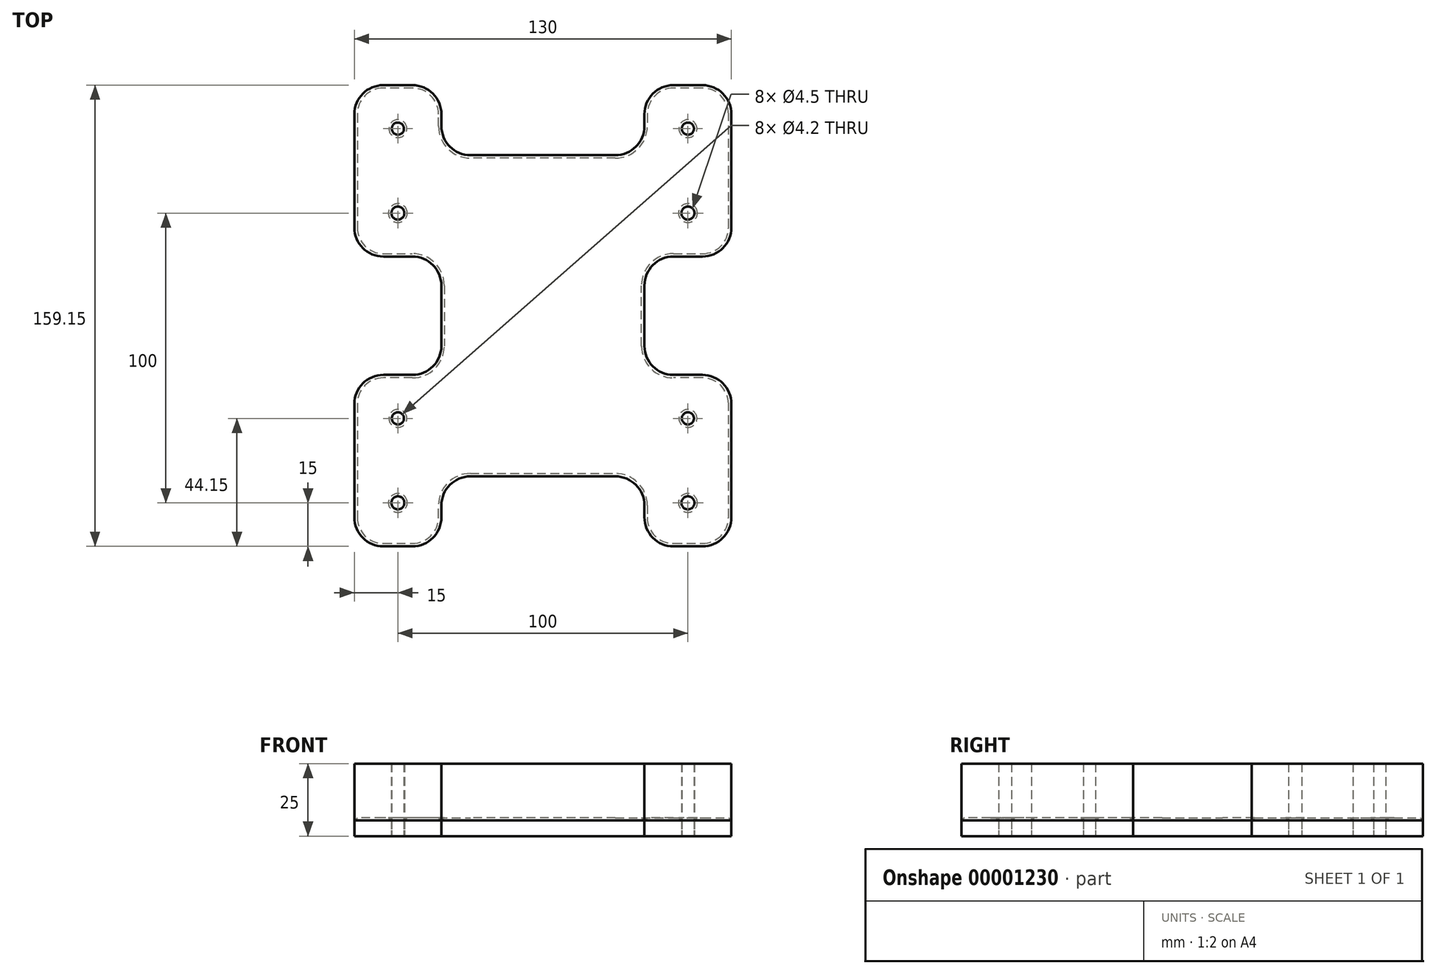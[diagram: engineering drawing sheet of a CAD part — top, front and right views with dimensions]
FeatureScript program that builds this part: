
annotation { "Feature Type Name" : "Feature", "Feature Type Description" : "" }
export const myFeature = defineFeature(function(context is Context, id is Id, definition is map)
    precondition{}
    {
        {
            var Q0;
            Q0=qCreatedBy(makeId("Top.planeOp"),FACE);
            var sketch = newSketch(context, id + "F0", { "sketchPlane" : qUnion([Q0])});
            skLineSegment(sketch, "E0", {"start": v(0, 159.15) * mm, "end": v(30, 159.15) * mm});
            skLineSegment(sketch, "E1", {"start": v(30, 159.15) * mm, "end": v(30, 135) * mm});
            skLineSegment(sketch, "E2", {"start": v(30, 135) * mm, "end": v(100, 135) * mm});
            skLineSegment(sketch, "E3", {"start": v(100, 135) * mm, "end": v(100, 159.15) * mm});
            skLineSegment(sketch, "E4", {"start": v(100, 159.15) * mm, "end": v(130, 159.15) * mm});
            skLineSegment(sketch, "E5", {"start": v(130, 159.15) * mm, "end": v(130, 100) * mm});
            skLineSegment(sketch, "E6", {"start": v(130, 100) * mm, "end": v(100, 100) * mm});
            skLineSegment(sketch, "E7", {"start": v(100, 100) * mm, "end": v(100, 59.15) * mm});
            skLineSegment(sketch, "E8", {"start": v(100, 59.15) * mm, "end": v(130, 59.15) * mm});
            skLineSegment(sketch, "E9", {"start": v(130, 59.15) * mm, "end": v(130, 0) * mm});
            skLineSegment(sketch, "E10", {"start": v(130, 0) * mm, "end": v(100, 0) * mm});
            skLineSegment(sketch, "E11", {"start": v(100, 0) * mm, "end": v(100, 24.15) * mm});
            skLineSegment(sketch, "E12", {"start": v(100, 24.15) * mm, "end": v(30, 24.15) * mm});
            skLineSegment(sketch, "E13", {"start": v(30, 24.15) * mm, "end": v(30, 0) * mm});
            skLineSegment(sketch, "E14", {"start": v(30, 0) * mm, "end": v(0, 0) * mm});
            skLineSegment(sketch, "E15", {"start": v(0, 0) * mm, "end": v(0, 59.15) * mm});
            skLineSegment(sketch, "E16", {"start": v(0, 59.15) * mm, "end": v(30, 59.15) * mm});
            skLineSegment(sketch, "E17", {"start": v(30, 59.15) * mm, "end": v(30, 100) * mm});
            skLineSegment(sketch, "E18", {"start": v(30, 100) * mm, "end": v(0, 100) * mm});
            skLineSegment(sketch, "E19", {"start": v(0, 100) * mm, "end": v(0, 159.15) * mm});
            skLineSegment(sketch, "E20", {"start": v(15, 159.15) * mm, "end": v(15, 144.15) * mm, "construction": true});
            skLineSegment(sketch, "E21", {"start": v(15, 100) * mm, "end": v(15, 115) * mm, "construction": true});
            skCircle(sketch, "E22", {"center": v(15, 144.15) * mm, "radius": 2.1 * mm});
            skCircle(sketch, "E23", {"center": v(15, 115) * mm, "radius": 2.25 * mm});
            skLineSegment(sketch, "E24", {"start": v(65, 135) * mm, "end": v(65, 24.15) * mm, "construction": true});
            skLineSegment(sketch, "E25", {"start": v(30, 79.57) * mm, "end": v(100, 79.57) * mm, "construction": true});
            skLineSegment(sketch, "E26", {"start": v(15, 59.15) * mm, "end": v(15, 44.15) * mm, "construction": true});
            skLineSegment(sketch, "E27", {"start": v(15, 0) * mm, "end": v(15, 15) * mm, "construction": true});
            skCircle(sketch, "E28", {"center": v(15, 44.15) * mm, "radius": 2.1 * mm});
            skCircle(sketch, "E29", {"center": v(15, 15) * mm, "radius": 2.25 * mm});
            skCircle(sketch, "E30.0.MirrorC", {"center": v(115, 15) * mm, "radius": 2.25 * mm});
            skCircle(sketch, "E30.1.MirrorC", {"center": v(115, 44.15) * mm, "radius": 2.1 * mm});
            skCircle(sketch, "E31.0.MirrorC", {"center": v(115, 115) * mm, "radius": 2.25 * mm});
            skCircle(sketch, "E31.1.MirrorC", {"center": v(115, 144.15) * mm, "radius": 2.1 * mm});
            skLineSegment(sketch, "E32", {"start": v(115, 144.15) * mm, "end": v(115, 44.15) * mm, "construction": true});
            skSolve(sketch);
        }
        {
            var Q0;
            Q0=makeQuery(id+"F0.imprint","IMPRINT",FACE,{"disambiguationData":[TD([[makeQuery(id+"F0.imprint","IMPRINT",EDGE,{"derivedFrom":sQuery(id+"F0.wireOp",EDGE,"E0")}),-1.0]])]});
            extrude(context, id + "F1", {"entities" : qUnion([Q0]), "depth" : 6.35 * mm});
        }
        {
            var Q0;
            Q0=makeQuery(id+"F1.opExtrude","SWEPT_EDGE",EDGE,{"disambiguationData":[OSD([sQuery(id+"F0.wireOp",EDGE,"E0"),sQuery(id+"F0.wireOp",EDGE,"E1")])]});
            var Q1;
            Q1=makeQuery(id+"F1.opExtrude","SWEPT_EDGE",EDGE,{"disambiguationData":[OSD([sQuery(id+"F0.wireOp",EDGE,"E0"),sQuery(id+"F0.wireOp",EDGE,"E19")])]});
            var Q2;
            Q2=makeQuery(id+"F1.opExtrude","SWEPT_EDGE",EDGE,{"disambiguationData":[OSD([sQuery(id+"F0.wireOp",EDGE,"E3"),sQuery(id+"F0.wireOp",EDGE,"E4")])]});
            var Q3;
            Q3=makeQuery(id+"F1.opExtrude","SWEPT_EDGE",EDGE,{"disambiguationData":[OSD([sQuery(id+"F0.wireOp",EDGE,"E4"),sQuery(id+"F0.wireOp",EDGE,"E5")])]});
            var Q4;
            Q4=makeQuery(id+"F1.opExtrude","SWEPT_EDGE",EDGE,{"disambiguationData":[OSD([sQuery(id+"F0.wireOp",EDGE,"E5"),sQuery(id+"F0.wireOp",EDGE,"E6")])]});
            var Q5;
            Q5=makeQuery(id+"F1.opExtrude","SWEPT_EDGE",EDGE,{"disambiguationData":[OSD([sQuery(id+"F0.wireOp",EDGE,"E7"),sQuery(id+"F0.wireOp",EDGE,"E8")])]});
            var Q6;
            Q6=makeQuery(id+"F1.opExtrude","SWEPT_EDGE",EDGE,{"disambiguationData":[OSD([sQuery(id+"F0.wireOp",EDGE,"E8"),sQuery(id+"F0.wireOp",EDGE,"E9")])]});
            var Q7;
            Q7=makeQuery(id+"F1.opExtrude","SWEPT_EDGE",EDGE,{"disambiguationData":[OSD([sQuery(id+"F0.wireOp",EDGE,"E9"),sQuery(id+"F0.wireOp",EDGE,"E10")])]});
            var Q8;
            Q8=makeQuery(id+"F1.opExtrude","SWEPT_EDGE",EDGE,{"disambiguationData":[OSD([sQuery(id+"F0.wireOp",EDGE,"E13"),sQuery(id+"F0.wireOp",EDGE,"E14")])]});
            var Q9;
            Q9=makeQuery(id+"F1.opExtrude","SWEPT_EDGE",EDGE,{"disambiguationData":[OSD([sQuery(id+"F0.wireOp",EDGE,"E15"),sQuery(id+"F0.wireOp",EDGE,"E16")])]});
            var Q10;
            Q10=makeQuery(id+"F1.opExtrude","SWEPT_EDGE",EDGE,{"disambiguationData":[OSD([sQuery(id+"F0.wireOp",EDGE,"E1"),sQuery(id+"F0.wireOp",EDGE,"E2")])]});
            var Q11;
            Q11=makeQuery(id+"F1.opExtrude","SWEPT_EDGE",EDGE,{"disambiguationData":[OSD([sQuery(id+"F0.wireOp",EDGE,"E2"),sQuery(id+"F0.wireOp",EDGE,"E3")])]});
            var Q12;
            Q12=makeQuery(id+"F1.opExtrude","SWEPT_EDGE",EDGE,{"disambiguationData":[OSD([sQuery(id+"F0.wireOp",EDGE,"E18"),sQuery(id+"F0.wireOp",EDGE,"E19")])]});
            var Q13;
            Q13=makeQuery(id+"F1.opExtrude","SWEPT_EDGE",EDGE,{"disambiguationData":[OSD([sQuery(id+"F0.wireOp",EDGE,"E10"),sQuery(id+"F0.wireOp",EDGE,"E11")])]});
            var Q14;
            Q14=makeQuery(id+"F1.opExtrude","SWEPT_EDGE",EDGE,{"disambiguationData":[OSD([sQuery(id+"F0.wireOp",EDGE,"E14"),sQuery(id+"F0.wireOp",EDGE,"E15")])]});
            var Q15;
            Q15=makeQuery(id+"F1.opExtrude","SWEPT_EDGE",EDGE,{"disambiguationData":[OSD([sQuery(id+"F0.wireOp",EDGE,"E16"),sQuery(id+"F0.wireOp",EDGE,"E17")])]});
            var Q16;
            Q16=makeQuery(id+"F1.opExtrude","SWEPT_EDGE",EDGE,{"disambiguationData":[OSD([sQuery(id+"F0.wireOp",EDGE,"E12"),sQuery(id+"F0.wireOp",EDGE,"E13")])]});
            var Q17;
            Q17=makeQuery(id+"F1.opExtrude","SWEPT_EDGE",EDGE,{"disambiguationData":[OSD([sQuery(id+"F0.wireOp",EDGE,"E6"),sQuery(id+"F0.wireOp",EDGE,"E7")])]});
            var Q18;
            Q18=makeQuery(id+"F1.opExtrude","SWEPT_EDGE",EDGE,{"disambiguationData":[OSD([sQuery(id+"F0.wireOp",EDGE,"E11"),sQuery(id+"F0.wireOp",EDGE,"E12")])]});
            var Q19;
            Q19=makeQuery(id+"F1.opExtrude","SWEPT_EDGE",EDGE,{"disambiguationData":[OSD([sQuery(id+"F0.wireOp",EDGE,"E17"),sQuery(id+"F0.wireOp",EDGE,"E18")])]});
            fillet(context, id + "F2", {"entities" : qUnion([Q0, Q1, Q2, Q3, Q4, Q5, Q6, Q7, Q8, Q9, Q10, Q11, Q12, Q13, Q14, Q15, Q16, Q17, Q18, Q19]), "radius" : 10 * mm, "tangentPropagation" : true, "allowEdgeOverflow" : false});
        }
        {
            var Q0;
            Q0=makeQuery(id+"F1.opExtrude","CAP_EDGE",EDGE,{"disambiguationData":[OSD([sQuery(id+"F0.wireOp",EDGE,"E12")])],"isStart":false});
            var Q1;
            {var subQ0=sQuery(id+"F0.wireOp",EDGE,"E13");var subQ1=sQuery(id+"F0.wireOp",EDGE,"E14");Q1=makeQuery(id+"F2.opFillet","BLEND_EDGE",EDGE,{"blendedFrom":[makeQuery(id+"F1.opExtrude","SWEPT_EDGE",EDGE,{"disambiguationData":[OSD([subQ0,subQ1])]}),makeQuery(id+"F1.opExtrude","CAP_FACE",FACE,{"disambiguationData":[OSD([sQuery(id+"F0.wireOp",EDGE,"E0"),sQuery(id+"F0.wireOp",EDGE,"E1"),sQuery(id+"F0.wireOp",EDGE,"E2"),sQuery(id+"F0.wireOp",EDGE,"E3"),sQuery(id+"F0.wireOp",EDGE,"E4"),sQuery(id+"F0.wireOp",EDGE,"E5"),sQuery(id+"F0.wireOp",EDGE,"E6"),sQuery(id+"F0.wireOp",EDGE,"E7"),sQuery(id+"F0.wireOp",EDGE,"E8"),sQuery(id+"F0.wireOp",EDGE,"E9"),sQuery(id+"F0.wireOp",EDGE,"E10"),sQuery(id+"F0.wireOp",EDGE,"E11"),sQuery(id+"F0.wireOp",EDGE,"E12"),subQ0,subQ1,sQuery(id+"F0.wireOp",EDGE,"E15"),sQuery(id+"F0.wireOp",EDGE,"E16"),sQuery(id+"F0.wireOp",EDGE,"E17"),sQuery(id+"F0.wireOp",EDGE,"E18"),sQuery(id+"F0.wireOp",EDGE,"E19"),sQuery(id+"F0.wireOp",EDGE,"E22"),sQuery(id+"F0.wireOp",EDGE,"E23"),sQuery(id+"F0.wireOp",EDGE,"E28"),sQuery(id+"F0.wireOp",EDGE,"E29"),sQuery(id+"F0.wireOp",EDGE,"E30.0.MirrorC"),sQuery(id+"F0.wireOp",EDGE,"E30.1.MirrorC"),sQuery(id+"F0.wireOp",EDGE,"E31.0.MirrorC"),sQuery(id+"F0.wireOp",EDGE,"E31.1.MirrorC")])],"isStart":false})],"blendedInto":[makeQuery(id+"F1.opExtrude","CAP_FACE",FACE,{"disambiguationData":[OSD([sQuery(id+"F0.wireOp",EDGE,"E0"),sQuery(id+"F0.wireOp",EDGE,"E1"),sQuery(id+"F0.wireOp",EDGE,"E2"),sQuery(id+"F0.wireOp",EDGE,"E3"),sQuery(id+"F0.wireOp",EDGE,"E4"),sQuery(id+"F0.wireOp",EDGE,"E5"),sQuery(id+"F0.wireOp",EDGE,"E6"),sQuery(id+"F0.wireOp",EDGE,"E7"),sQuery(id+"F0.wireOp",EDGE,"E8"),sQuery(id+"F0.wireOp",EDGE,"E9"),sQuery(id+"F0.wireOp",EDGE,"E10"),sQuery(id+"F0.wireOp",EDGE,"E11"),sQuery(id+"F0.wireOp",EDGE,"E12"),subQ0,subQ1,sQuery(id+"F0.wireOp",EDGE,"E15"),sQuery(id+"F0.wireOp",EDGE,"E16"),sQuery(id+"F0.wireOp",EDGE,"E17"),sQuery(id+"F0.wireOp",EDGE,"E18"),sQuery(id+"F0.wireOp",EDGE,"E19"),sQuery(id+"F0.wireOp",EDGE,"E22"),sQuery(id+"F0.wireOp",EDGE,"E23"),sQuery(id+"F0.wireOp",EDGE,"E28"),sQuery(id+"F0.wireOp",EDGE,"E29"),sQuery(id+"F0.wireOp",EDGE,"E30.0.MirrorC"),sQuery(id+"F0.wireOp",EDGE,"E30.1.MirrorC"),sQuery(id+"F0.wireOp",EDGE,"E31.0.MirrorC"),sQuery(id+"F0.wireOp",EDGE,"E31.1.MirrorC")])],"isStart":false})]});}
            var Q2;
            {var subQ0=sQuery(id+"F0.wireOp",EDGE,"E10");var subQ1=sQuery(id+"F0.wireOp",EDGE,"E11");Q2=makeQuery(id+"F2.opFillet","BLEND_EDGE",EDGE,{"blendedFrom":[makeQuery(id+"F1.opExtrude","SWEPT_EDGE",EDGE,{"disambiguationData":[OSD([subQ0,subQ1])]}),makeQuery(id+"F1.opExtrude","CAP_FACE",FACE,{"disambiguationData":[OSD([sQuery(id+"F0.wireOp",EDGE,"E0"),sQuery(id+"F0.wireOp",EDGE,"E1"),sQuery(id+"F0.wireOp",EDGE,"E2"),sQuery(id+"F0.wireOp",EDGE,"E3"),sQuery(id+"F0.wireOp",EDGE,"E4"),sQuery(id+"F0.wireOp",EDGE,"E5"),sQuery(id+"F0.wireOp",EDGE,"E6"),sQuery(id+"F0.wireOp",EDGE,"E7"),sQuery(id+"F0.wireOp",EDGE,"E8"),sQuery(id+"F0.wireOp",EDGE,"E9"),subQ0,subQ1,sQuery(id+"F0.wireOp",EDGE,"E12"),sQuery(id+"F0.wireOp",EDGE,"E13"),sQuery(id+"F0.wireOp",EDGE,"E14"),sQuery(id+"F0.wireOp",EDGE,"E15"),sQuery(id+"F0.wireOp",EDGE,"E16"),sQuery(id+"F0.wireOp",EDGE,"E17"),sQuery(id+"F0.wireOp",EDGE,"E18"),sQuery(id+"F0.wireOp",EDGE,"E19"),sQuery(id+"F0.wireOp",EDGE,"E22"),sQuery(id+"F0.wireOp",EDGE,"E23"),sQuery(id+"F0.wireOp",EDGE,"E28"),sQuery(id+"F0.wireOp",EDGE,"E29"),sQuery(id+"F0.wireOp",EDGE,"E30.0.MirrorC"),sQuery(id+"F0.wireOp",EDGE,"E30.1.MirrorC"),sQuery(id+"F0.wireOp",EDGE,"E31.0.MirrorC"),sQuery(id+"F0.wireOp",EDGE,"E31.1.MirrorC")])],"isStart":false})],"blendedInto":[makeQuery(id+"F1.opExtrude","CAP_FACE",FACE,{"disambiguationData":[OSD([sQuery(id+"F0.wireOp",EDGE,"E0"),sQuery(id+"F0.wireOp",EDGE,"E1"),sQuery(id+"F0.wireOp",EDGE,"E2"),sQuery(id+"F0.wireOp",EDGE,"E3"),sQuery(id+"F0.wireOp",EDGE,"E4"),sQuery(id+"F0.wireOp",EDGE,"E5"),sQuery(id+"F0.wireOp",EDGE,"E6"),sQuery(id+"F0.wireOp",EDGE,"E7"),sQuery(id+"F0.wireOp",EDGE,"E8"),sQuery(id+"F0.wireOp",EDGE,"E9"),subQ0,subQ1,sQuery(id+"F0.wireOp",EDGE,"E12"),sQuery(id+"F0.wireOp",EDGE,"E13"),sQuery(id+"F0.wireOp",EDGE,"E14"),sQuery(id+"F0.wireOp",EDGE,"E15"),sQuery(id+"F0.wireOp",EDGE,"E16"),sQuery(id+"F0.wireOp",EDGE,"E17"),sQuery(id+"F0.wireOp",EDGE,"E18"),sQuery(id+"F0.wireOp",EDGE,"E19"),sQuery(id+"F0.wireOp",EDGE,"E22"),sQuery(id+"F0.wireOp",EDGE,"E23"),sQuery(id+"F0.wireOp",EDGE,"E28"),sQuery(id+"F0.wireOp",EDGE,"E29"),sQuery(id+"F0.wireOp",EDGE,"E30.0.MirrorC"),sQuery(id+"F0.wireOp",EDGE,"E30.1.MirrorC"),sQuery(id+"F0.wireOp",EDGE,"E31.0.MirrorC"),sQuery(id+"F0.wireOp",EDGE,"E31.1.MirrorC")])],"isStart":false})]});}
            var Q3;
            {var subQ0=sQuery(id+"F0.wireOp",EDGE,"E9");var subQ1=sQuery(id+"F0.wireOp",EDGE,"E10");Q3=makeQuery(id+"F2.opFillet","BLEND_EDGE",EDGE,{"blendedFrom":[makeQuery(id+"F1.opExtrude","SWEPT_EDGE",EDGE,{"disambiguationData":[OSD([subQ0,subQ1])]}),makeQuery(id+"F1.opExtrude","CAP_FACE",FACE,{"disambiguationData":[OSD([sQuery(id+"F0.wireOp",EDGE,"E0"),sQuery(id+"F0.wireOp",EDGE,"E1"),sQuery(id+"F0.wireOp",EDGE,"E2"),sQuery(id+"F0.wireOp",EDGE,"E3"),sQuery(id+"F0.wireOp",EDGE,"E4"),sQuery(id+"F0.wireOp",EDGE,"E5"),sQuery(id+"F0.wireOp",EDGE,"E6"),sQuery(id+"F0.wireOp",EDGE,"E7"),sQuery(id+"F0.wireOp",EDGE,"E8"),subQ0,subQ1,sQuery(id+"F0.wireOp",EDGE,"E11"),sQuery(id+"F0.wireOp",EDGE,"E12"),sQuery(id+"F0.wireOp",EDGE,"E13"),sQuery(id+"F0.wireOp",EDGE,"E14"),sQuery(id+"F0.wireOp",EDGE,"E15"),sQuery(id+"F0.wireOp",EDGE,"E16"),sQuery(id+"F0.wireOp",EDGE,"E17"),sQuery(id+"F0.wireOp",EDGE,"E18"),sQuery(id+"F0.wireOp",EDGE,"E19"),sQuery(id+"F0.wireOp",EDGE,"E22"),sQuery(id+"F0.wireOp",EDGE,"E23"),sQuery(id+"F0.wireOp",EDGE,"E28"),sQuery(id+"F0.wireOp",EDGE,"E29"),sQuery(id+"F0.wireOp",EDGE,"E30.0.MirrorC"),sQuery(id+"F0.wireOp",EDGE,"E30.1.MirrorC"),sQuery(id+"F0.wireOp",EDGE,"E31.0.MirrorC"),sQuery(id+"F0.wireOp",EDGE,"E31.1.MirrorC")])],"isStart":false})],"blendedInto":[makeQuery(id+"F1.opExtrude","CAP_FACE",FACE,{"disambiguationData":[OSD([sQuery(id+"F0.wireOp",EDGE,"E0"),sQuery(id+"F0.wireOp",EDGE,"E1"),sQuery(id+"F0.wireOp",EDGE,"E2"),sQuery(id+"F0.wireOp",EDGE,"E3"),sQuery(id+"F0.wireOp",EDGE,"E4"),sQuery(id+"F0.wireOp",EDGE,"E5"),sQuery(id+"F0.wireOp",EDGE,"E6"),sQuery(id+"F0.wireOp",EDGE,"E7"),sQuery(id+"F0.wireOp",EDGE,"E8"),subQ0,subQ1,sQuery(id+"F0.wireOp",EDGE,"E11"),sQuery(id+"F0.wireOp",EDGE,"E12"),sQuery(id+"F0.wireOp",EDGE,"E13"),sQuery(id+"F0.wireOp",EDGE,"E14"),sQuery(id+"F0.wireOp",EDGE,"E15"),sQuery(id+"F0.wireOp",EDGE,"E16"),sQuery(id+"F0.wireOp",EDGE,"E17"),sQuery(id+"F0.wireOp",EDGE,"E18"),sQuery(id+"F0.wireOp",EDGE,"E19"),sQuery(id+"F0.wireOp",EDGE,"E22"),sQuery(id+"F0.wireOp",EDGE,"E23"),sQuery(id+"F0.wireOp",EDGE,"E28"),sQuery(id+"F0.wireOp",EDGE,"E29"),sQuery(id+"F0.wireOp",EDGE,"E30.0.MirrorC"),sQuery(id+"F0.wireOp",EDGE,"E30.1.MirrorC"),sQuery(id+"F0.wireOp",EDGE,"E31.0.MirrorC"),sQuery(id+"F0.wireOp",EDGE,"E31.1.MirrorC")])],"isStart":false})]});}
            var Q4;
            {var subQ0=sQuery(id+"F0.wireOp",EDGE,"E11");var subQ1=sQuery(id+"F0.wireOp",EDGE,"E12");Q4=makeQuery(id+"F2.opFillet","BLEND_EDGE",EDGE,{"blendedFrom":[makeQuery(id+"F1.opExtrude","SWEPT_EDGE",EDGE,{"disambiguationData":[OSD([subQ0,subQ1])]}),makeQuery(id+"F1.opExtrude","CAP_FACE",FACE,{"disambiguationData":[OSD([sQuery(id+"F0.wireOp",EDGE,"E0"),sQuery(id+"F0.wireOp",EDGE,"E1"),sQuery(id+"F0.wireOp",EDGE,"E2"),sQuery(id+"F0.wireOp",EDGE,"E3"),sQuery(id+"F0.wireOp",EDGE,"E4"),sQuery(id+"F0.wireOp",EDGE,"E5"),sQuery(id+"F0.wireOp",EDGE,"E6"),sQuery(id+"F0.wireOp",EDGE,"E7"),sQuery(id+"F0.wireOp",EDGE,"E8"),sQuery(id+"F0.wireOp",EDGE,"E9"),sQuery(id+"F0.wireOp",EDGE,"E10"),subQ0,subQ1,sQuery(id+"F0.wireOp",EDGE,"E13"),sQuery(id+"F0.wireOp",EDGE,"E14"),sQuery(id+"F0.wireOp",EDGE,"E15"),sQuery(id+"F0.wireOp",EDGE,"E16"),sQuery(id+"F0.wireOp",EDGE,"E17"),sQuery(id+"F0.wireOp",EDGE,"E18"),sQuery(id+"F0.wireOp",EDGE,"E19"),sQuery(id+"F0.wireOp",EDGE,"E22"),sQuery(id+"F0.wireOp",EDGE,"E23"),sQuery(id+"F0.wireOp",EDGE,"E28"),sQuery(id+"F0.wireOp",EDGE,"E29"),sQuery(id+"F0.wireOp",EDGE,"E30.0.MirrorC"),sQuery(id+"F0.wireOp",EDGE,"E30.1.MirrorC"),sQuery(id+"F0.wireOp",EDGE,"E31.0.MirrorC"),sQuery(id+"F0.wireOp",EDGE,"E31.1.MirrorC")])],"isStart":false})],"blendedInto":[makeQuery(id+"F1.opExtrude","CAP_FACE",FACE,{"disambiguationData":[OSD([sQuery(id+"F0.wireOp",EDGE,"E0"),sQuery(id+"F0.wireOp",EDGE,"E1"),sQuery(id+"F0.wireOp",EDGE,"E2"),sQuery(id+"F0.wireOp",EDGE,"E3"),sQuery(id+"F0.wireOp",EDGE,"E4"),sQuery(id+"F0.wireOp",EDGE,"E5"),sQuery(id+"F0.wireOp",EDGE,"E6"),sQuery(id+"F0.wireOp",EDGE,"E7"),sQuery(id+"F0.wireOp",EDGE,"E8"),sQuery(id+"F0.wireOp",EDGE,"E9"),sQuery(id+"F0.wireOp",EDGE,"E10"),subQ0,subQ1,sQuery(id+"F0.wireOp",EDGE,"E13"),sQuery(id+"F0.wireOp",EDGE,"E14"),sQuery(id+"F0.wireOp",EDGE,"E15"),sQuery(id+"F0.wireOp",EDGE,"E16"),sQuery(id+"F0.wireOp",EDGE,"E17"),sQuery(id+"F0.wireOp",EDGE,"E18"),sQuery(id+"F0.wireOp",EDGE,"E19"),sQuery(id+"F0.wireOp",EDGE,"E22"),sQuery(id+"F0.wireOp",EDGE,"E23"),sQuery(id+"F0.wireOp",EDGE,"E28"),sQuery(id+"F0.wireOp",EDGE,"E29"),sQuery(id+"F0.wireOp",EDGE,"E30.0.MirrorC"),sQuery(id+"F0.wireOp",EDGE,"E30.1.MirrorC"),sQuery(id+"F0.wireOp",EDGE,"E31.0.MirrorC"),sQuery(id+"F0.wireOp",EDGE,"E31.1.MirrorC")])],"isStart":false})]});}
            var Q5;
            {var subQ0=sQuery(id+"F0.wireOp",EDGE,"E14");var subQ1=sQuery(id+"F0.wireOp",EDGE,"E15");Q5=makeQuery(id+"F2.opFillet","BLEND_EDGE",EDGE,{"blendedFrom":[makeQuery(id+"F1.opExtrude","SWEPT_EDGE",EDGE,{"disambiguationData":[OSD([subQ0,subQ1])]}),makeQuery(id+"F1.opExtrude","CAP_FACE",FACE,{"disambiguationData":[OSD([sQuery(id+"F0.wireOp",EDGE,"E0"),sQuery(id+"F0.wireOp",EDGE,"E1"),sQuery(id+"F0.wireOp",EDGE,"E2"),sQuery(id+"F0.wireOp",EDGE,"E3"),sQuery(id+"F0.wireOp",EDGE,"E4"),sQuery(id+"F0.wireOp",EDGE,"E5"),sQuery(id+"F0.wireOp",EDGE,"E6"),sQuery(id+"F0.wireOp",EDGE,"E7"),sQuery(id+"F0.wireOp",EDGE,"E8"),sQuery(id+"F0.wireOp",EDGE,"E9"),sQuery(id+"F0.wireOp",EDGE,"E10"),sQuery(id+"F0.wireOp",EDGE,"E11"),sQuery(id+"F0.wireOp",EDGE,"E12"),sQuery(id+"F0.wireOp",EDGE,"E13"),subQ0,subQ1,sQuery(id+"F0.wireOp",EDGE,"E16"),sQuery(id+"F0.wireOp",EDGE,"E17"),sQuery(id+"F0.wireOp",EDGE,"E18"),sQuery(id+"F0.wireOp",EDGE,"E19"),sQuery(id+"F0.wireOp",EDGE,"E22"),sQuery(id+"F0.wireOp",EDGE,"E23"),sQuery(id+"F0.wireOp",EDGE,"E28"),sQuery(id+"F0.wireOp",EDGE,"E29"),sQuery(id+"F0.wireOp",EDGE,"E30.0.MirrorC"),sQuery(id+"F0.wireOp",EDGE,"E30.1.MirrorC"),sQuery(id+"F0.wireOp",EDGE,"E31.0.MirrorC"),sQuery(id+"F0.wireOp",EDGE,"E31.1.MirrorC")])],"isStart":false})],"blendedInto":[makeQuery(id+"F1.opExtrude","CAP_FACE",FACE,{"disambiguationData":[OSD([sQuery(id+"F0.wireOp",EDGE,"E0"),sQuery(id+"F0.wireOp",EDGE,"E1"),sQuery(id+"F0.wireOp",EDGE,"E2"),sQuery(id+"F0.wireOp",EDGE,"E3"),sQuery(id+"F0.wireOp",EDGE,"E4"),sQuery(id+"F0.wireOp",EDGE,"E5"),sQuery(id+"F0.wireOp",EDGE,"E6"),sQuery(id+"F0.wireOp",EDGE,"E7"),sQuery(id+"F0.wireOp",EDGE,"E8"),sQuery(id+"F0.wireOp",EDGE,"E9"),sQuery(id+"F0.wireOp",EDGE,"E10"),sQuery(id+"F0.wireOp",EDGE,"E11"),sQuery(id+"F0.wireOp",EDGE,"E12"),sQuery(id+"F0.wireOp",EDGE,"E13"),subQ0,subQ1,sQuery(id+"F0.wireOp",EDGE,"E16"),sQuery(id+"F0.wireOp",EDGE,"E17"),sQuery(id+"F0.wireOp",EDGE,"E18"),sQuery(id+"F0.wireOp",EDGE,"E19"),sQuery(id+"F0.wireOp",EDGE,"E22"),sQuery(id+"F0.wireOp",EDGE,"E23"),sQuery(id+"F0.wireOp",EDGE,"E28"),sQuery(id+"F0.wireOp",EDGE,"E29"),sQuery(id+"F0.wireOp",EDGE,"E30.0.MirrorC"),sQuery(id+"F0.wireOp",EDGE,"E30.1.MirrorC"),sQuery(id+"F0.wireOp",EDGE,"E31.0.MirrorC"),sQuery(id+"F0.wireOp",EDGE,"E31.1.MirrorC")])],"isStart":false})]});}
            var Q6;
            Q6=makeQuery(id+"F1.opExtrude","CAP_EDGE",EDGE,{"disambiguationData":[OSD([sQuery(id+"F0.wireOp",EDGE,"E14")])],"isStart":false});
            var Q7;
            Q7=makeQuery(id+"F1.opExtrude","CAP_EDGE",EDGE,{"disambiguationData":[OSD([sQuery(id+"F0.wireOp",EDGE,"E10")])],"isStart":false});
            var Q8;
            {var subQ0=sQuery(id+"F0.wireOp",EDGE,"E12");var subQ1=sQuery(id+"F0.wireOp",EDGE,"E13");Q8=makeQuery(id+"F2.opFillet","BLEND_EDGE",EDGE,{"blendedFrom":[makeQuery(id+"F1.opExtrude","SWEPT_EDGE",EDGE,{"disambiguationData":[OSD([subQ0,subQ1])]}),makeQuery(id+"F1.opExtrude","CAP_FACE",FACE,{"disambiguationData":[OSD([sQuery(id+"F0.wireOp",EDGE,"E0"),sQuery(id+"F0.wireOp",EDGE,"E1"),sQuery(id+"F0.wireOp",EDGE,"E2"),sQuery(id+"F0.wireOp",EDGE,"E3"),sQuery(id+"F0.wireOp",EDGE,"E4"),sQuery(id+"F0.wireOp",EDGE,"E5"),sQuery(id+"F0.wireOp",EDGE,"E6"),sQuery(id+"F0.wireOp",EDGE,"E7"),sQuery(id+"F0.wireOp",EDGE,"E8"),sQuery(id+"F0.wireOp",EDGE,"E9"),sQuery(id+"F0.wireOp",EDGE,"E10"),sQuery(id+"F0.wireOp",EDGE,"E11"),subQ0,subQ1,sQuery(id+"F0.wireOp",EDGE,"E14"),sQuery(id+"F0.wireOp",EDGE,"E15"),sQuery(id+"F0.wireOp",EDGE,"E16"),sQuery(id+"F0.wireOp",EDGE,"E17"),sQuery(id+"F0.wireOp",EDGE,"E18"),sQuery(id+"F0.wireOp",EDGE,"E19"),sQuery(id+"F0.wireOp",EDGE,"E22"),sQuery(id+"F0.wireOp",EDGE,"E23"),sQuery(id+"F0.wireOp",EDGE,"E28"),sQuery(id+"F0.wireOp",EDGE,"E29"),sQuery(id+"F0.wireOp",EDGE,"E30.0.MirrorC"),sQuery(id+"F0.wireOp",EDGE,"E30.1.MirrorC"),sQuery(id+"F0.wireOp",EDGE,"E31.0.MirrorC"),sQuery(id+"F0.wireOp",EDGE,"E31.1.MirrorC")])],"isStart":false})],"blendedInto":[makeQuery(id+"F1.opExtrude","CAP_FACE",FACE,{"disambiguationData":[OSD([sQuery(id+"F0.wireOp",EDGE,"E0"),sQuery(id+"F0.wireOp",EDGE,"E1"),sQuery(id+"F0.wireOp",EDGE,"E2"),sQuery(id+"F0.wireOp",EDGE,"E3"),sQuery(id+"F0.wireOp",EDGE,"E4"),sQuery(id+"F0.wireOp",EDGE,"E5"),sQuery(id+"F0.wireOp",EDGE,"E6"),sQuery(id+"F0.wireOp",EDGE,"E7"),sQuery(id+"F0.wireOp",EDGE,"E8"),sQuery(id+"F0.wireOp",EDGE,"E9"),sQuery(id+"F0.wireOp",EDGE,"E10"),sQuery(id+"F0.wireOp",EDGE,"E11"),subQ0,subQ1,sQuery(id+"F0.wireOp",EDGE,"E14"),sQuery(id+"F0.wireOp",EDGE,"E15"),sQuery(id+"F0.wireOp",EDGE,"E16"),sQuery(id+"F0.wireOp",EDGE,"E17"),sQuery(id+"F0.wireOp",EDGE,"E18"),sQuery(id+"F0.wireOp",EDGE,"E19"),sQuery(id+"F0.wireOp",EDGE,"E22"),sQuery(id+"F0.wireOp",EDGE,"E23"),sQuery(id+"F0.wireOp",EDGE,"E28"),sQuery(id+"F0.wireOp",EDGE,"E29"),sQuery(id+"F0.wireOp",EDGE,"E30.0.MirrorC"),sQuery(id+"F0.wireOp",EDGE,"E30.1.MirrorC"),sQuery(id+"F0.wireOp",EDGE,"E31.0.MirrorC"),sQuery(id+"F0.wireOp",EDGE,"E31.1.MirrorC")])],"isStart":false})]});}
            var Q9;
            Q9=makeQuery(id+"F1.opExtrude","CAP_EDGE",EDGE,{"disambiguationData":[OSD([sQuery(id+"F0.wireOp",EDGE,"E30.0.MirrorC")])],"isStart":false});
            var Q10;
            Q10=makeQuery(id+"F1.opExtrude","CAP_EDGE",EDGE,{"disambiguationData":[OSD([sQuery(id+"F0.wireOp",EDGE,"E16")])],"isStart":false});
            var Q11;
            {var subQ0=sQuery(id+"F0.wireOp",EDGE,"E8");var subQ1=sQuery(id+"F0.wireOp",EDGE,"E9");Q11=makeQuery(id+"F2.opFillet","BLEND_EDGE",EDGE,{"blendedFrom":[makeQuery(id+"F1.opExtrude","SWEPT_EDGE",EDGE,{"disambiguationData":[OSD([subQ0,subQ1])]}),makeQuery(id+"F1.opExtrude","CAP_FACE",FACE,{"disambiguationData":[OSD([sQuery(id+"F0.wireOp",EDGE,"E0"),sQuery(id+"F0.wireOp",EDGE,"E1"),sQuery(id+"F0.wireOp",EDGE,"E2"),sQuery(id+"F0.wireOp",EDGE,"E3"),sQuery(id+"F0.wireOp",EDGE,"E4"),sQuery(id+"F0.wireOp",EDGE,"E5"),sQuery(id+"F0.wireOp",EDGE,"E6"),sQuery(id+"F0.wireOp",EDGE,"E7"),subQ0,subQ1,sQuery(id+"F0.wireOp",EDGE,"E10"),sQuery(id+"F0.wireOp",EDGE,"E11"),sQuery(id+"F0.wireOp",EDGE,"E12"),sQuery(id+"F0.wireOp",EDGE,"E13"),sQuery(id+"F0.wireOp",EDGE,"E14"),sQuery(id+"F0.wireOp",EDGE,"E15"),sQuery(id+"F0.wireOp",EDGE,"E16"),sQuery(id+"F0.wireOp",EDGE,"E17"),sQuery(id+"F0.wireOp",EDGE,"E18"),sQuery(id+"F0.wireOp",EDGE,"E19"),sQuery(id+"F0.wireOp",EDGE,"E22"),sQuery(id+"F0.wireOp",EDGE,"E23"),sQuery(id+"F0.wireOp",EDGE,"E28"),sQuery(id+"F0.wireOp",EDGE,"E29"),sQuery(id+"F0.wireOp",EDGE,"E30.0.MirrorC"),sQuery(id+"F0.wireOp",EDGE,"E30.1.MirrorC"),sQuery(id+"F0.wireOp",EDGE,"E31.0.MirrorC"),sQuery(id+"F0.wireOp",EDGE,"E31.1.MirrorC")])],"isStart":false})],"blendedInto":[makeQuery(id+"F1.opExtrude","CAP_FACE",FACE,{"disambiguationData":[OSD([sQuery(id+"F0.wireOp",EDGE,"E0"),sQuery(id+"F0.wireOp",EDGE,"E1"),sQuery(id+"F0.wireOp",EDGE,"E2"),sQuery(id+"F0.wireOp",EDGE,"E3"),sQuery(id+"F0.wireOp",EDGE,"E4"),sQuery(id+"F0.wireOp",EDGE,"E5"),sQuery(id+"F0.wireOp",EDGE,"E6"),sQuery(id+"F0.wireOp",EDGE,"E7"),subQ0,subQ1,sQuery(id+"F0.wireOp",EDGE,"E10"),sQuery(id+"F0.wireOp",EDGE,"E11"),sQuery(id+"F0.wireOp",EDGE,"E12"),sQuery(id+"F0.wireOp",EDGE,"E13"),sQuery(id+"F0.wireOp",EDGE,"E14"),sQuery(id+"F0.wireOp",EDGE,"E15"),sQuery(id+"F0.wireOp",EDGE,"E16"),sQuery(id+"F0.wireOp",EDGE,"E17"),sQuery(id+"F0.wireOp",EDGE,"E18"),sQuery(id+"F0.wireOp",EDGE,"E19"),sQuery(id+"F0.wireOp",EDGE,"E22"),sQuery(id+"F0.wireOp",EDGE,"E23"),sQuery(id+"F0.wireOp",EDGE,"E28"),sQuery(id+"F0.wireOp",EDGE,"E29"),sQuery(id+"F0.wireOp",EDGE,"E30.0.MirrorC"),sQuery(id+"F0.wireOp",EDGE,"E30.1.MirrorC"),sQuery(id+"F0.wireOp",EDGE,"E31.0.MirrorC"),sQuery(id+"F0.wireOp",EDGE,"E31.1.MirrorC")])],"isStart":false})]});}
            var Q12;
            Q12=makeQuery(id+"F1.opExtrude","CAP_EDGE",EDGE,{"disambiguationData":[OSD([sQuery(id+"F0.wireOp",EDGE,"E15")])],"isStart":false});
            var Q13;
            Q13=makeQuery(id+"F1.opExtrude","CAP_EDGE",EDGE,{"disambiguationData":[OSD([sQuery(id+"F0.wireOp",EDGE,"E29")])],"isStart":false});
            var Q14;
            Q14=makeQuery(id+"F1.opExtrude","CAP_EDGE",EDGE,{"disambiguationData":[OSD([sQuery(id+"F0.wireOp",EDGE,"E9")])],"isStart":false});
            var Q15;
            {var subQ0=sQuery(id+"F0.wireOp",EDGE,"E1");var subQ1=sQuery(id+"F0.wireOp",EDGE,"E2");Q15=makeQuery(id+"F2.opFillet","BLEND_EDGE",EDGE,{"blendedFrom":[makeQuery(id+"F1.opExtrude","SWEPT_EDGE",EDGE,{"disambiguationData":[OSD([subQ0,subQ1])]}),makeQuery(id+"F1.opExtrude","CAP_FACE",FACE,{"disambiguationData":[OSD([sQuery(id+"F0.wireOp",EDGE,"E0"),subQ0,subQ1,sQuery(id+"F0.wireOp",EDGE,"E3"),sQuery(id+"F0.wireOp",EDGE,"E4"),sQuery(id+"F0.wireOp",EDGE,"E5"),sQuery(id+"F0.wireOp",EDGE,"E6"),sQuery(id+"F0.wireOp",EDGE,"E7"),sQuery(id+"F0.wireOp",EDGE,"E8"),sQuery(id+"F0.wireOp",EDGE,"E9"),sQuery(id+"F0.wireOp",EDGE,"E10"),sQuery(id+"F0.wireOp",EDGE,"E11"),sQuery(id+"F0.wireOp",EDGE,"E12"),sQuery(id+"F0.wireOp",EDGE,"E13"),sQuery(id+"F0.wireOp",EDGE,"E14"),sQuery(id+"F0.wireOp",EDGE,"E15"),sQuery(id+"F0.wireOp",EDGE,"E16"),sQuery(id+"F0.wireOp",EDGE,"E17"),sQuery(id+"F0.wireOp",EDGE,"E18"),sQuery(id+"F0.wireOp",EDGE,"E19"),sQuery(id+"F0.wireOp",EDGE,"E22"),sQuery(id+"F0.wireOp",EDGE,"E23"),sQuery(id+"F0.wireOp",EDGE,"E28"),sQuery(id+"F0.wireOp",EDGE,"E29"),sQuery(id+"F0.wireOp",EDGE,"E30.0.MirrorC"),sQuery(id+"F0.wireOp",EDGE,"E30.1.MirrorC"),sQuery(id+"F0.wireOp",EDGE,"E31.0.MirrorC"),sQuery(id+"F0.wireOp",EDGE,"E31.1.MirrorC")])],"isStart":false})],"blendedInto":[makeQuery(id+"F1.opExtrude","CAP_FACE",FACE,{"disambiguationData":[OSD([sQuery(id+"F0.wireOp",EDGE,"E0"),subQ0,subQ1,sQuery(id+"F0.wireOp",EDGE,"E3"),sQuery(id+"F0.wireOp",EDGE,"E4"),sQuery(id+"F0.wireOp",EDGE,"E5"),sQuery(id+"F0.wireOp",EDGE,"E6"),sQuery(id+"F0.wireOp",EDGE,"E7"),sQuery(id+"F0.wireOp",EDGE,"E8"),sQuery(id+"F0.wireOp",EDGE,"E9"),sQuery(id+"F0.wireOp",EDGE,"E10"),sQuery(id+"F0.wireOp",EDGE,"E11"),sQuery(id+"F0.wireOp",EDGE,"E12"),sQuery(id+"F0.wireOp",EDGE,"E13"),sQuery(id+"F0.wireOp",EDGE,"E14"),sQuery(id+"F0.wireOp",EDGE,"E15"),sQuery(id+"F0.wireOp",EDGE,"E16"),sQuery(id+"F0.wireOp",EDGE,"E17"),sQuery(id+"F0.wireOp",EDGE,"E18"),sQuery(id+"F0.wireOp",EDGE,"E19"),sQuery(id+"F0.wireOp",EDGE,"E22"),sQuery(id+"F0.wireOp",EDGE,"E23"),sQuery(id+"F0.wireOp",EDGE,"E28"),sQuery(id+"F0.wireOp",EDGE,"E29"),sQuery(id+"F0.wireOp",EDGE,"E30.0.MirrorC"),sQuery(id+"F0.wireOp",EDGE,"E30.1.MirrorC"),sQuery(id+"F0.wireOp",EDGE,"E31.0.MirrorC"),sQuery(id+"F0.wireOp",EDGE,"E31.1.MirrorC")])],"isStart":false})]});}
            var Q16;
            Q16=makeQuery(id+"F1.opExtrude","CAP_EDGE",EDGE,{"disambiguationData":[OSD([sQuery(id+"F0.wireOp",EDGE,"E13")])],"isStart":false});
            var Q17;
            Q17=makeQuery(id+"F1.opExtrude","CAP_EDGE",EDGE,{"disambiguationData":[OSD([sQuery(id+"F0.wireOp",EDGE,"E8")])],"isStart":false});
            var Q18;
            Q18=makeQuery(id+"F1.opExtrude","CAP_EDGE",EDGE,{"disambiguationData":[OSD([sQuery(id+"F0.wireOp",EDGE,"E11")])],"isStart":false});
            var Q19;
            {var subQ0=sQuery(id+"F0.wireOp",EDGE,"E7");var subQ1=sQuery(id+"F0.wireOp",EDGE,"E8");Q19=makeQuery(id+"F2.opFillet","BLEND_EDGE",EDGE,{"blendedFrom":[makeQuery(id+"F1.opExtrude","SWEPT_EDGE",EDGE,{"disambiguationData":[OSD([subQ0,subQ1])]}),makeQuery(id+"F1.opExtrude","CAP_FACE",FACE,{"disambiguationData":[OSD([sQuery(id+"F0.wireOp",EDGE,"E0"),sQuery(id+"F0.wireOp",EDGE,"E1"),sQuery(id+"F0.wireOp",EDGE,"E2"),sQuery(id+"F0.wireOp",EDGE,"E3"),sQuery(id+"F0.wireOp",EDGE,"E4"),sQuery(id+"F0.wireOp",EDGE,"E5"),sQuery(id+"F0.wireOp",EDGE,"E6"),subQ0,subQ1,sQuery(id+"F0.wireOp",EDGE,"E9"),sQuery(id+"F0.wireOp",EDGE,"E10"),sQuery(id+"F0.wireOp",EDGE,"E11"),sQuery(id+"F0.wireOp",EDGE,"E12"),sQuery(id+"F0.wireOp",EDGE,"E13"),sQuery(id+"F0.wireOp",EDGE,"E14"),sQuery(id+"F0.wireOp",EDGE,"E15"),sQuery(id+"F0.wireOp",EDGE,"E16"),sQuery(id+"F0.wireOp",EDGE,"E17"),sQuery(id+"F0.wireOp",EDGE,"E18"),sQuery(id+"F0.wireOp",EDGE,"E19"),sQuery(id+"F0.wireOp",EDGE,"E22"),sQuery(id+"F0.wireOp",EDGE,"E23"),sQuery(id+"F0.wireOp",EDGE,"E28"),sQuery(id+"F0.wireOp",EDGE,"E29"),sQuery(id+"F0.wireOp",EDGE,"E30.0.MirrorC"),sQuery(id+"F0.wireOp",EDGE,"E30.1.MirrorC"),sQuery(id+"F0.wireOp",EDGE,"E31.0.MirrorC"),sQuery(id+"F0.wireOp",EDGE,"E31.1.MirrorC")])],"isStart":false})],"blendedInto":[makeQuery(id+"F1.opExtrude","CAP_FACE",FACE,{"disambiguationData":[OSD([sQuery(id+"F0.wireOp",EDGE,"E0"),sQuery(id+"F0.wireOp",EDGE,"E1"),sQuery(id+"F0.wireOp",EDGE,"E2"),sQuery(id+"F0.wireOp",EDGE,"E3"),sQuery(id+"F0.wireOp",EDGE,"E4"),sQuery(id+"F0.wireOp",EDGE,"E5"),sQuery(id+"F0.wireOp",EDGE,"E6"),subQ0,subQ1,sQuery(id+"F0.wireOp",EDGE,"E9"),sQuery(id+"F0.wireOp",EDGE,"E10"),sQuery(id+"F0.wireOp",EDGE,"E11"),sQuery(id+"F0.wireOp",EDGE,"E12"),sQuery(id+"F0.wireOp",EDGE,"E13"),sQuery(id+"F0.wireOp",EDGE,"E14"),sQuery(id+"F0.wireOp",EDGE,"E15"),sQuery(id+"F0.wireOp",EDGE,"E16"),sQuery(id+"F0.wireOp",EDGE,"E17"),sQuery(id+"F0.wireOp",EDGE,"E18"),sQuery(id+"F0.wireOp",EDGE,"E19"),sQuery(id+"F0.wireOp",EDGE,"E22"),sQuery(id+"F0.wireOp",EDGE,"E23"),sQuery(id+"F0.wireOp",EDGE,"E28"),sQuery(id+"F0.wireOp",EDGE,"E29"),sQuery(id+"F0.wireOp",EDGE,"E30.0.MirrorC"),sQuery(id+"F0.wireOp",EDGE,"E30.1.MirrorC"),sQuery(id+"F0.wireOp",EDGE,"E31.0.MirrorC"),sQuery(id+"F0.wireOp",EDGE,"E31.1.MirrorC")])],"isStart":false})]});}
            var Q20;
            {var subQ0=sQuery(id+"F0.wireOp",EDGE,"E2");var subQ1=sQuery(id+"F0.wireOp",EDGE,"E3");Q20=makeQuery(id+"F2.opFillet","BLEND_EDGE",EDGE,{"blendedFrom":[makeQuery(id+"F1.opExtrude","SWEPT_EDGE",EDGE,{"disambiguationData":[OSD([subQ0,subQ1])]}),makeQuery(id+"F1.opExtrude","CAP_FACE",FACE,{"disambiguationData":[OSD([sQuery(id+"F0.wireOp",EDGE,"E0"),sQuery(id+"F0.wireOp",EDGE,"E1"),subQ0,subQ1,sQuery(id+"F0.wireOp",EDGE,"E4"),sQuery(id+"F0.wireOp",EDGE,"E5"),sQuery(id+"F0.wireOp",EDGE,"E6"),sQuery(id+"F0.wireOp",EDGE,"E7"),sQuery(id+"F0.wireOp",EDGE,"E8"),sQuery(id+"F0.wireOp",EDGE,"E9"),sQuery(id+"F0.wireOp",EDGE,"E10"),sQuery(id+"F0.wireOp",EDGE,"E11"),sQuery(id+"F0.wireOp",EDGE,"E12"),sQuery(id+"F0.wireOp",EDGE,"E13"),sQuery(id+"F0.wireOp",EDGE,"E14"),sQuery(id+"F0.wireOp",EDGE,"E15"),sQuery(id+"F0.wireOp",EDGE,"E16"),sQuery(id+"F0.wireOp",EDGE,"E17"),sQuery(id+"F0.wireOp",EDGE,"E18"),sQuery(id+"F0.wireOp",EDGE,"E19"),sQuery(id+"F0.wireOp",EDGE,"E22"),sQuery(id+"F0.wireOp",EDGE,"E23"),sQuery(id+"F0.wireOp",EDGE,"E28"),sQuery(id+"F0.wireOp",EDGE,"E29"),sQuery(id+"F0.wireOp",EDGE,"E30.0.MirrorC"),sQuery(id+"F0.wireOp",EDGE,"E30.1.MirrorC"),sQuery(id+"F0.wireOp",EDGE,"E31.0.MirrorC"),sQuery(id+"F0.wireOp",EDGE,"E31.1.MirrorC")])],"isStart":false})],"blendedInto":[makeQuery(id+"F1.opExtrude","CAP_FACE",FACE,{"disambiguationData":[OSD([sQuery(id+"F0.wireOp",EDGE,"E0"),sQuery(id+"F0.wireOp",EDGE,"E1"),subQ0,subQ1,sQuery(id+"F0.wireOp",EDGE,"E4"),sQuery(id+"F0.wireOp",EDGE,"E5"),sQuery(id+"F0.wireOp",EDGE,"E6"),sQuery(id+"F0.wireOp",EDGE,"E7"),sQuery(id+"F0.wireOp",EDGE,"E8"),sQuery(id+"F0.wireOp",EDGE,"E9"),sQuery(id+"F0.wireOp",EDGE,"E10"),sQuery(id+"F0.wireOp",EDGE,"E11"),sQuery(id+"F0.wireOp",EDGE,"E12"),sQuery(id+"F0.wireOp",EDGE,"E13"),sQuery(id+"F0.wireOp",EDGE,"E14"),sQuery(id+"F0.wireOp",EDGE,"E15"),sQuery(id+"F0.wireOp",EDGE,"E16"),sQuery(id+"F0.wireOp",EDGE,"E17"),sQuery(id+"F0.wireOp",EDGE,"E18"),sQuery(id+"F0.wireOp",EDGE,"E19"),sQuery(id+"F0.wireOp",EDGE,"E22"),sQuery(id+"F0.wireOp",EDGE,"E23"),sQuery(id+"F0.wireOp",EDGE,"E28"),sQuery(id+"F0.wireOp",EDGE,"E29"),sQuery(id+"F0.wireOp",EDGE,"E30.0.MirrorC"),sQuery(id+"F0.wireOp",EDGE,"E30.1.MirrorC"),sQuery(id+"F0.wireOp",EDGE,"E31.0.MirrorC"),sQuery(id+"F0.wireOp",EDGE,"E31.1.MirrorC")])],"isStart":false})]});}
            var Q21;
            {var subQ0=sQuery(id+"F0.wireOp",EDGE,"E16");var subQ1=sQuery(id+"F0.wireOp",EDGE,"E17");Q21=makeQuery(id+"F2.opFillet","BLEND_EDGE",EDGE,{"blendedFrom":[makeQuery(id+"F1.opExtrude","SWEPT_EDGE",EDGE,{"disambiguationData":[OSD([subQ0,subQ1])]}),makeQuery(id+"F1.opExtrude","CAP_FACE",FACE,{"disambiguationData":[OSD([sQuery(id+"F0.wireOp",EDGE,"E0"),sQuery(id+"F0.wireOp",EDGE,"E1"),sQuery(id+"F0.wireOp",EDGE,"E2"),sQuery(id+"F0.wireOp",EDGE,"E3"),sQuery(id+"F0.wireOp",EDGE,"E4"),sQuery(id+"F0.wireOp",EDGE,"E5"),sQuery(id+"F0.wireOp",EDGE,"E6"),sQuery(id+"F0.wireOp",EDGE,"E7"),sQuery(id+"F0.wireOp",EDGE,"E8"),sQuery(id+"F0.wireOp",EDGE,"E9"),sQuery(id+"F0.wireOp",EDGE,"E10"),sQuery(id+"F0.wireOp",EDGE,"E11"),sQuery(id+"F0.wireOp",EDGE,"E12"),sQuery(id+"F0.wireOp",EDGE,"E13"),sQuery(id+"F0.wireOp",EDGE,"E14"),sQuery(id+"F0.wireOp",EDGE,"E15"),subQ0,subQ1,sQuery(id+"F0.wireOp",EDGE,"E18"),sQuery(id+"F0.wireOp",EDGE,"E19"),sQuery(id+"F0.wireOp",EDGE,"E22"),sQuery(id+"F0.wireOp",EDGE,"E23"),sQuery(id+"F0.wireOp",EDGE,"E28"),sQuery(id+"F0.wireOp",EDGE,"E29"),sQuery(id+"F0.wireOp",EDGE,"E30.0.MirrorC"),sQuery(id+"F0.wireOp",EDGE,"E30.1.MirrorC"),sQuery(id+"F0.wireOp",EDGE,"E31.0.MirrorC"),sQuery(id+"F0.wireOp",EDGE,"E31.1.MirrorC")])],"isStart":false})],"blendedInto":[makeQuery(id+"F1.opExtrude","CAP_FACE",FACE,{"disambiguationData":[OSD([sQuery(id+"F0.wireOp",EDGE,"E0"),sQuery(id+"F0.wireOp",EDGE,"E1"),sQuery(id+"F0.wireOp",EDGE,"E2"),sQuery(id+"F0.wireOp",EDGE,"E3"),sQuery(id+"F0.wireOp",EDGE,"E4"),sQuery(id+"F0.wireOp",EDGE,"E5"),sQuery(id+"F0.wireOp",EDGE,"E6"),sQuery(id+"F0.wireOp",EDGE,"E7"),sQuery(id+"F0.wireOp",EDGE,"E8"),sQuery(id+"F0.wireOp",EDGE,"E9"),sQuery(id+"F0.wireOp",EDGE,"E10"),sQuery(id+"F0.wireOp",EDGE,"E11"),sQuery(id+"F0.wireOp",EDGE,"E12"),sQuery(id+"F0.wireOp",EDGE,"E13"),sQuery(id+"F0.wireOp",EDGE,"E14"),sQuery(id+"F0.wireOp",EDGE,"E15"),subQ0,subQ1,sQuery(id+"F0.wireOp",EDGE,"E18"),sQuery(id+"F0.wireOp",EDGE,"E19"),sQuery(id+"F0.wireOp",EDGE,"E22"),sQuery(id+"F0.wireOp",EDGE,"E23"),sQuery(id+"F0.wireOp",EDGE,"E28"),sQuery(id+"F0.wireOp",EDGE,"E29"),sQuery(id+"F0.wireOp",EDGE,"E30.0.MirrorC"),sQuery(id+"F0.wireOp",EDGE,"E30.1.MirrorC"),sQuery(id+"F0.wireOp",EDGE,"E31.0.MirrorC"),sQuery(id+"F0.wireOp",EDGE,"E31.1.MirrorC")])],"isStart":false})]});}
            var Q22;
            Q22=makeQuery(id+"F1.opExtrude","CAP_EDGE",EDGE,{"disambiguationData":[OSD([sQuery(id+"F0.wireOp",EDGE,"E2")])],"isStart":false});
            var Q23;
            {var subQ0=sQuery(id+"F0.wireOp",EDGE,"E15");var subQ1=sQuery(id+"F0.wireOp",EDGE,"E16");Q23=makeQuery(id+"F2.opFillet","BLEND_EDGE",EDGE,{"blendedFrom":[makeQuery(id+"F1.opExtrude","SWEPT_EDGE",EDGE,{"disambiguationData":[OSD([subQ0,subQ1])]}),makeQuery(id+"F1.opExtrude","CAP_FACE",FACE,{"disambiguationData":[OSD([sQuery(id+"F0.wireOp",EDGE,"E0"),sQuery(id+"F0.wireOp",EDGE,"E1"),sQuery(id+"F0.wireOp",EDGE,"E2"),sQuery(id+"F0.wireOp",EDGE,"E3"),sQuery(id+"F0.wireOp",EDGE,"E4"),sQuery(id+"F0.wireOp",EDGE,"E5"),sQuery(id+"F0.wireOp",EDGE,"E6"),sQuery(id+"F0.wireOp",EDGE,"E7"),sQuery(id+"F0.wireOp",EDGE,"E8"),sQuery(id+"F0.wireOp",EDGE,"E9"),sQuery(id+"F0.wireOp",EDGE,"E10"),sQuery(id+"F0.wireOp",EDGE,"E11"),sQuery(id+"F0.wireOp",EDGE,"E12"),sQuery(id+"F0.wireOp",EDGE,"E13"),sQuery(id+"F0.wireOp",EDGE,"E14"),subQ0,subQ1,sQuery(id+"F0.wireOp",EDGE,"E17"),sQuery(id+"F0.wireOp",EDGE,"E18"),sQuery(id+"F0.wireOp",EDGE,"E19"),sQuery(id+"F0.wireOp",EDGE,"E22"),sQuery(id+"F0.wireOp",EDGE,"E23"),sQuery(id+"F0.wireOp",EDGE,"E28"),sQuery(id+"F0.wireOp",EDGE,"E29"),sQuery(id+"F0.wireOp",EDGE,"E30.0.MirrorC"),sQuery(id+"F0.wireOp",EDGE,"E30.1.MirrorC"),sQuery(id+"F0.wireOp",EDGE,"E31.0.MirrorC"),sQuery(id+"F0.wireOp",EDGE,"E31.1.MirrorC")])],"isStart":false})],"blendedInto":[makeQuery(id+"F1.opExtrude","CAP_FACE",FACE,{"disambiguationData":[OSD([sQuery(id+"F0.wireOp",EDGE,"E0"),sQuery(id+"F0.wireOp",EDGE,"E1"),sQuery(id+"F0.wireOp",EDGE,"E2"),sQuery(id+"F0.wireOp",EDGE,"E3"),sQuery(id+"F0.wireOp",EDGE,"E4"),sQuery(id+"F0.wireOp",EDGE,"E5"),sQuery(id+"F0.wireOp",EDGE,"E6"),sQuery(id+"F0.wireOp",EDGE,"E7"),sQuery(id+"F0.wireOp",EDGE,"E8"),sQuery(id+"F0.wireOp",EDGE,"E9"),sQuery(id+"F0.wireOp",EDGE,"E10"),sQuery(id+"F0.wireOp",EDGE,"E11"),sQuery(id+"F0.wireOp",EDGE,"E12"),sQuery(id+"F0.wireOp",EDGE,"E13"),sQuery(id+"F0.wireOp",EDGE,"E14"),subQ0,subQ1,sQuery(id+"F0.wireOp",EDGE,"E17"),sQuery(id+"F0.wireOp",EDGE,"E18"),sQuery(id+"F0.wireOp",EDGE,"E19"),sQuery(id+"F0.wireOp",EDGE,"E22"),sQuery(id+"F0.wireOp",EDGE,"E23"),sQuery(id+"F0.wireOp",EDGE,"E28"),sQuery(id+"F0.wireOp",EDGE,"E29"),sQuery(id+"F0.wireOp",EDGE,"E30.0.MirrorC"),sQuery(id+"F0.wireOp",EDGE,"E30.1.MirrorC"),sQuery(id+"F0.wireOp",EDGE,"E31.0.MirrorC"),sQuery(id+"F0.wireOp",EDGE,"E31.1.MirrorC")])],"isStart":false})]});}
            var Q24;
            {var subQ0=sQuery(id+"F0.wireOp",EDGE,"E6");var subQ1=sQuery(id+"F0.wireOp",EDGE,"E7");Q24=makeQuery(id+"F2.opFillet","BLEND_EDGE",EDGE,{"blendedFrom":[makeQuery(id+"F1.opExtrude","SWEPT_EDGE",EDGE,{"disambiguationData":[OSD([subQ0,subQ1])]}),makeQuery(id+"F1.opExtrude","CAP_FACE",FACE,{"disambiguationData":[OSD([sQuery(id+"F0.wireOp",EDGE,"E0"),sQuery(id+"F0.wireOp",EDGE,"E1"),sQuery(id+"F0.wireOp",EDGE,"E2"),sQuery(id+"F0.wireOp",EDGE,"E3"),sQuery(id+"F0.wireOp",EDGE,"E4"),sQuery(id+"F0.wireOp",EDGE,"E5"),subQ0,subQ1,sQuery(id+"F0.wireOp",EDGE,"E8"),sQuery(id+"F0.wireOp",EDGE,"E9"),sQuery(id+"F0.wireOp",EDGE,"E10"),sQuery(id+"F0.wireOp",EDGE,"E11"),sQuery(id+"F0.wireOp",EDGE,"E12"),sQuery(id+"F0.wireOp",EDGE,"E13"),sQuery(id+"F0.wireOp",EDGE,"E14"),sQuery(id+"F0.wireOp",EDGE,"E15"),sQuery(id+"F0.wireOp",EDGE,"E16"),sQuery(id+"F0.wireOp",EDGE,"E17"),sQuery(id+"F0.wireOp",EDGE,"E18"),sQuery(id+"F0.wireOp",EDGE,"E19"),sQuery(id+"F0.wireOp",EDGE,"E22"),sQuery(id+"F0.wireOp",EDGE,"E23"),sQuery(id+"F0.wireOp",EDGE,"E28"),sQuery(id+"F0.wireOp",EDGE,"E29"),sQuery(id+"F0.wireOp",EDGE,"E30.0.MirrorC"),sQuery(id+"F0.wireOp",EDGE,"E30.1.MirrorC"),sQuery(id+"F0.wireOp",EDGE,"E31.0.MirrorC"),sQuery(id+"F0.wireOp",EDGE,"E31.1.MirrorC")])],"isStart":false})],"blendedInto":[makeQuery(id+"F1.opExtrude","CAP_FACE",FACE,{"disambiguationData":[OSD([sQuery(id+"F0.wireOp",EDGE,"E0"),sQuery(id+"F0.wireOp",EDGE,"E1"),sQuery(id+"F0.wireOp",EDGE,"E2"),sQuery(id+"F0.wireOp",EDGE,"E3"),sQuery(id+"F0.wireOp",EDGE,"E4"),sQuery(id+"F0.wireOp",EDGE,"E5"),subQ0,subQ1,sQuery(id+"F0.wireOp",EDGE,"E8"),sQuery(id+"F0.wireOp",EDGE,"E9"),sQuery(id+"F0.wireOp",EDGE,"E10"),sQuery(id+"F0.wireOp",EDGE,"E11"),sQuery(id+"F0.wireOp",EDGE,"E12"),sQuery(id+"F0.wireOp",EDGE,"E13"),sQuery(id+"F0.wireOp",EDGE,"E14"),sQuery(id+"F0.wireOp",EDGE,"E15"),sQuery(id+"F0.wireOp",EDGE,"E16"),sQuery(id+"F0.wireOp",EDGE,"E17"),sQuery(id+"F0.wireOp",EDGE,"E18"),sQuery(id+"F0.wireOp",EDGE,"E19"),sQuery(id+"F0.wireOp",EDGE,"E22"),sQuery(id+"F0.wireOp",EDGE,"E23"),sQuery(id+"F0.wireOp",EDGE,"E28"),sQuery(id+"F0.wireOp",EDGE,"E29"),sQuery(id+"F0.wireOp",EDGE,"E30.0.MirrorC"),sQuery(id+"F0.wireOp",EDGE,"E30.1.MirrorC"),sQuery(id+"F0.wireOp",EDGE,"E31.0.MirrorC"),sQuery(id+"F0.wireOp",EDGE,"E31.1.MirrorC")])],"isStart":false})]});}
            var Q25;
            Q25=makeQuery(id+"F1.opExtrude","CAP_EDGE",EDGE,{"disambiguationData":[OSD([sQuery(id+"F0.wireOp",EDGE,"E30.1.MirrorC")])],"isStart":false});
            var Q26;
            {var subQ0=sQuery(id+"F0.wireOp",EDGE,"E17");var subQ1=sQuery(id+"F0.wireOp",EDGE,"E18");Q26=makeQuery(id+"F2.opFillet","BLEND_EDGE",EDGE,{"blendedFrom":[makeQuery(id+"F1.opExtrude","SWEPT_EDGE",EDGE,{"disambiguationData":[OSD([subQ0,subQ1])]}),makeQuery(id+"F1.opExtrude","CAP_FACE",FACE,{"disambiguationData":[OSD([sQuery(id+"F0.wireOp",EDGE,"E0"),sQuery(id+"F0.wireOp",EDGE,"E1"),sQuery(id+"F0.wireOp",EDGE,"E2"),sQuery(id+"F0.wireOp",EDGE,"E3"),sQuery(id+"F0.wireOp",EDGE,"E4"),sQuery(id+"F0.wireOp",EDGE,"E5"),sQuery(id+"F0.wireOp",EDGE,"E6"),sQuery(id+"F0.wireOp",EDGE,"E7"),sQuery(id+"F0.wireOp",EDGE,"E8"),sQuery(id+"F0.wireOp",EDGE,"E9"),sQuery(id+"F0.wireOp",EDGE,"E10"),sQuery(id+"F0.wireOp",EDGE,"E11"),sQuery(id+"F0.wireOp",EDGE,"E12"),sQuery(id+"F0.wireOp",EDGE,"E13"),sQuery(id+"F0.wireOp",EDGE,"E14"),sQuery(id+"F0.wireOp",EDGE,"E15"),sQuery(id+"F0.wireOp",EDGE,"E16"),subQ0,subQ1,sQuery(id+"F0.wireOp",EDGE,"E19"),sQuery(id+"F0.wireOp",EDGE,"E22"),sQuery(id+"F0.wireOp",EDGE,"E23"),sQuery(id+"F0.wireOp",EDGE,"E28"),sQuery(id+"F0.wireOp",EDGE,"E29"),sQuery(id+"F0.wireOp",EDGE,"E30.0.MirrorC"),sQuery(id+"F0.wireOp",EDGE,"E30.1.MirrorC"),sQuery(id+"F0.wireOp",EDGE,"E31.0.MirrorC"),sQuery(id+"F0.wireOp",EDGE,"E31.1.MirrorC")])],"isStart":false})],"blendedInto":[makeQuery(id+"F1.opExtrude","CAP_FACE",FACE,{"disambiguationData":[OSD([sQuery(id+"F0.wireOp",EDGE,"E0"),sQuery(id+"F0.wireOp",EDGE,"E1"),sQuery(id+"F0.wireOp",EDGE,"E2"),sQuery(id+"F0.wireOp",EDGE,"E3"),sQuery(id+"F0.wireOp",EDGE,"E4"),sQuery(id+"F0.wireOp",EDGE,"E5"),sQuery(id+"F0.wireOp",EDGE,"E6"),sQuery(id+"F0.wireOp",EDGE,"E7"),sQuery(id+"F0.wireOp",EDGE,"E8"),sQuery(id+"F0.wireOp",EDGE,"E9"),sQuery(id+"F0.wireOp",EDGE,"E10"),sQuery(id+"F0.wireOp",EDGE,"E11"),sQuery(id+"F0.wireOp",EDGE,"E12"),sQuery(id+"F0.wireOp",EDGE,"E13"),sQuery(id+"F0.wireOp",EDGE,"E14"),sQuery(id+"F0.wireOp",EDGE,"E15"),sQuery(id+"F0.wireOp",EDGE,"E16"),subQ0,subQ1,sQuery(id+"F0.wireOp",EDGE,"E19"),sQuery(id+"F0.wireOp",EDGE,"E22"),sQuery(id+"F0.wireOp",EDGE,"E23"),sQuery(id+"F0.wireOp",EDGE,"E28"),sQuery(id+"F0.wireOp",EDGE,"E29"),sQuery(id+"F0.wireOp",EDGE,"E30.0.MirrorC"),sQuery(id+"F0.wireOp",EDGE,"E30.1.MirrorC"),sQuery(id+"F0.wireOp",EDGE,"E31.0.MirrorC"),sQuery(id+"F0.wireOp",EDGE,"E31.1.MirrorC")])],"isStart":false})]});}
            var Q27;
            Q27=makeQuery(id+"F1.opExtrude","CAP_EDGE",EDGE,{"disambiguationData":[OSD([sQuery(id+"F0.wireOp",EDGE,"E28")])],"isStart":false});
            var Q28;
            Q28=makeQuery(id+"F1.opExtrude","CAP_EDGE",EDGE,{"disambiguationData":[OSD([sQuery(id+"F0.wireOp",EDGE,"E17")])],"isStart":false});
            var Q29;
            {var subQ0=sQuery(id+"F0.wireOp",EDGE,"E5");var subQ1=sQuery(id+"F0.wireOp",EDGE,"E6");Q29=makeQuery(id+"F2.opFillet","BLEND_EDGE",EDGE,{"blendedFrom":[makeQuery(id+"F1.opExtrude","SWEPT_EDGE",EDGE,{"disambiguationData":[OSD([subQ0,subQ1])]}),makeQuery(id+"F1.opExtrude","CAP_FACE",FACE,{"disambiguationData":[OSD([sQuery(id+"F0.wireOp",EDGE,"E0"),sQuery(id+"F0.wireOp",EDGE,"E1"),sQuery(id+"F0.wireOp",EDGE,"E2"),sQuery(id+"F0.wireOp",EDGE,"E3"),sQuery(id+"F0.wireOp",EDGE,"E4"),subQ0,subQ1,sQuery(id+"F0.wireOp",EDGE,"E7"),sQuery(id+"F0.wireOp",EDGE,"E8"),sQuery(id+"F0.wireOp",EDGE,"E9"),sQuery(id+"F0.wireOp",EDGE,"E10"),sQuery(id+"F0.wireOp",EDGE,"E11"),sQuery(id+"F0.wireOp",EDGE,"E12"),sQuery(id+"F0.wireOp",EDGE,"E13"),sQuery(id+"F0.wireOp",EDGE,"E14"),sQuery(id+"F0.wireOp",EDGE,"E15"),sQuery(id+"F0.wireOp",EDGE,"E16"),sQuery(id+"F0.wireOp",EDGE,"E17"),sQuery(id+"F0.wireOp",EDGE,"E18"),sQuery(id+"F0.wireOp",EDGE,"E19"),sQuery(id+"F0.wireOp",EDGE,"E22"),sQuery(id+"F0.wireOp",EDGE,"E23"),sQuery(id+"F0.wireOp",EDGE,"E28"),sQuery(id+"F0.wireOp",EDGE,"E29"),sQuery(id+"F0.wireOp",EDGE,"E30.0.MirrorC"),sQuery(id+"F0.wireOp",EDGE,"E30.1.MirrorC"),sQuery(id+"F0.wireOp",EDGE,"E31.0.MirrorC"),sQuery(id+"F0.wireOp",EDGE,"E31.1.MirrorC")])],"isStart":false})],"blendedInto":[makeQuery(id+"F1.opExtrude","CAP_FACE",FACE,{"disambiguationData":[OSD([sQuery(id+"F0.wireOp",EDGE,"E0"),sQuery(id+"F0.wireOp",EDGE,"E1"),sQuery(id+"F0.wireOp",EDGE,"E2"),sQuery(id+"F0.wireOp",EDGE,"E3"),sQuery(id+"F0.wireOp",EDGE,"E4"),subQ0,subQ1,sQuery(id+"F0.wireOp",EDGE,"E7"),sQuery(id+"F0.wireOp",EDGE,"E8"),sQuery(id+"F0.wireOp",EDGE,"E9"),sQuery(id+"F0.wireOp",EDGE,"E10"),sQuery(id+"F0.wireOp",EDGE,"E11"),sQuery(id+"F0.wireOp",EDGE,"E12"),sQuery(id+"F0.wireOp",EDGE,"E13"),sQuery(id+"F0.wireOp",EDGE,"E14"),sQuery(id+"F0.wireOp",EDGE,"E15"),sQuery(id+"F0.wireOp",EDGE,"E16"),sQuery(id+"F0.wireOp",EDGE,"E17"),sQuery(id+"F0.wireOp",EDGE,"E18"),sQuery(id+"F0.wireOp",EDGE,"E19"),sQuery(id+"F0.wireOp",EDGE,"E22"),sQuery(id+"F0.wireOp",EDGE,"E23"),sQuery(id+"F0.wireOp",EDGE,"E28"),sQuery(id+"F0.wireOp",EDGE,"E29"),sQuery(id+"F0.wireOp",EDGE,"E30.0.MirrorC"),sQuery(id+"F0.wireOp",EDGE,"E30.1.MirrorC"),sQuery(id+"F0.wireOp",EDGE,"E31.0.MirrorC"),sQuery(id+"F0.wireOp",EDGE,"E31.1.MirrorC")])],"isStart":false})]});}
            var Q30;
            Q30=makeQuery(id+"F1.opExtrude","CAP_EDGE",EDGE,{"disambiguationData":[OSD([sQuery(id+"F0.wireOp",EDGE,"E7")])],"isStart":false});
            var Q31;
            {var subQ0=sQuery(id+"F0.wireOp",EDGE,"E18");var subQ1=sQuery(id+"F0.wireOp",EDGE,"E19");Q31=makeQuery(id+"F2.opFillet","BLEND_EDGE",EDGE,{"blendedFrom":[makeQuery(id+"F1.opExtrude","SWEPT_EDGE",EDGE,{"disambiguationData":[OSD([subQ0,subQ1])]}),makeQuery(id+"F1.opExtrude","CAP_FACE",FACE,{"disambiguationData":[OSD([sQuery(id+"F0.wireOp",EDGE,"E0"),sQuery(id+"F0.wireOp",EDGE,"E1"),sQuery(id+"F0.wireOp",EDGE,"E2"),sQuery(id+"F0.wireOp",EDGE,"E3"),sQuery(id+"F0.wireOp",EDGE,"E4"),sQuery(id+"F0.wireOp",EDGE,"E5"),sQuery(id+"F0.wireOp",EDGE,"E6"),sQuery(id+"F0.wireOp",EDGE,"E7"),sQuery(id+"F0.wireOp",EDGE,"E8"),sQuery(id+"F0.wireOp",EDGE,"E9"),sQuery(id+"F0.wireOp",EDGE,"E10"),sQuery(id+"F0.wireOp",EDGE,"E11"),sQuery(id+"F0.wireOp",EDGE,"E12"),sQuery(id+"F0.wireOp",EDGE,"E13"),sQuery(id+"F0.wireOp",EDGE,"E14"),sQuery(id+"F0.wireOp",EDGE,"E15"),sQuery(id+"F0.wireOp",EDGE,"E16"),sQuery(id+"F0.wireOp",EDGE,"E17"),subQ0,subQ1,sQuery(id+"F0.wireOp",EDGE,"E22"),sQuery(id+"F0.wireOp",EDGE,"E23"),sQuery(id+"F0.wireOp",EDGE,"E28"),sQuery(id+"F0.wireOp",EDGE,"E29"),sQuery(id+"F0.wireOp",EDGE,"E30.0.MirrorC"),sQuery(id+"F0.wireOp",EDGE,"E30.1.MirrorC"),sQuery(id+"F0.wireOp",EDGE,"E31.0.MirrorC"),sQuery(id+"F0.wireOp",EDGE,"E31.1.MirrorC")])],"isStart":false})],"blendedInto":[makeQuery(id+"F1.opExtrude","CAP_FACE",FACE,{"disambiguationData":[OSD([sQuery(id+"F0.wireOp",EDGE,"E0"),sQuery(id+"F0.wireOp",EDGE,"E1"),sQuery(id+"F0.wireOp",EDGE,"E2"),sQuery(id+"F0.wireOp",EDGE,"E3"),sQuery(id+"F0.wireOp",EDGE,"E4"),sQuery(id+"F0.wireOp",EDGE,"E5"),sQuery(id+"F0.wireOp",EDGE,"E6"),sQuery(id+"F0.wireOp",EDGE,"E7"),sQuery(id+"F0.wireOp",EDGE,"E8"),sQuery(id+"F0.wireOp",EDGE,"E9"),sQuery(id+"F0.wireOp",EDGE,"E10"),sQuery(id+"F0.wireOp",EDGE,"E11"),sQuery(id+"F0.wireOp",EDGE,"E12"),sQuery(id+"F0.wireOp",EDGE,"E13"),sQuery(id+"F0.wireOp",EDGE,"E14"),sQuery(id+"F0.wireOp",EDGE,"E15"),sQuery(id+"F0.wireOp",EDGE,"E16"),sQuery(id+"F0.wireOp",EDGE,"E17"),subQ0,subQ1,sQuery(id+"F0.wireOp",EDGE,"E22"),sQuery(id+"F0.wireOp",EDGE,"E23"),sQuery(id+"F0.wireOp",EDGE,"E28"),sQuery(id+"F0.wireOp",EDGE,"E29"),sQuery(id+"F0.wireOp",EDGE,"E30.0.MirrorC"),sQuery(id+"F0.wireOp",EDGE,"E30.1.MirrorC"),sQuery(id+"F0.wireOp",EDGE,"E31.0.MirrorC"),sQuery(id+"F0.wireOp",EDGE,"E31.1.MirrorC")])],"isStart":false})]});}
            var Q32;
            Q32=makeQuery(id+"F1.opExtrude","CAP_EDGE",EDGE,{"disambiguationData":[OSD([sQuery(id+"F0.wireOp",EDGE,"E18")])],"isStart":false});
            var Q33;
            Q33=makeQuery(id+"F1.opExtrude","CAP_EDGE",EDGE,{"disambiguationData":[OSD([sQuery(id+"F0.wireOp",EDGE,"E6")])],"isStart":false});
            var Q34;
            Q34=makeQuery(id+"F1.opExtrude","CAP_EDGE",EDGE,{"disambiguationData":[OSD([sQuery(id+"F0.wireOp",EDGE,"E31.0.MirrorC")])],"isStart":false});
            var Q35;
            {var subQ0=sQuery(id+"F0.wireOp",EDGE,"E0");var subQ1=sQuery(id+"F0.wireOp",EDGE,"E1");Q35=makeQuery(id+"F2.opFillet","BLEND_EDGE",EDGE,{"blendedFrom":[makeQuery(id+"F1.opExtrude","SWEPT_EDGE",EDGE,{"disambiguationData":[OSD([subQ0,subQ1])]}),makeQuery(id+"F1.opExtrude","CAP_FACE",FACE,{"disambiguationData":[OSD([subQ0,subQ1,sQuery(id+"F0.wireOp",EDGE,"E2"),sQuery(id+"F0.wireOp",EDGE,"E3"),sQuery(id+"F0.wireOp",EDGE,"E4"),sQuery(id+"F0.wireOp",EDGE,"E5"),sQuery(id+"F0.wireOp",EDGE,"E6"),sQuery(id+"F0.wireOp",EDGE,"E7"),sQuery(id+"F0.wireOp",EDGE,"E8"),sQuery(id+"F0.wireOp",EDGE,"E9"),sQuery(id+"F0.wireOp",EDGE,"E10"),sQuery(id+"F0.wireOp",EDGE,"E11"),sQuery(id+"F0.wireOp",EDGE,"E12"),sQuery(id+"F0.wireOp",EDGE,"E13"),sQuery(id+"F0.wireOp",EDGE,"E14"),sQuery(id+"F0.wireOp",EDGE,"E15"),sQuery(id+"F0.wireOp",EDGE,"E16"),sQuery(id+"F0.wireOp",EDGE,"E17"),sQuery(id+"F0.wireOp",EDGE,"E18"),sQuery(id+"F0.wireOp",EDGE,"E19"),sQuery(id+"F0.wireOp",EDGE,"E22"),sQuery(id+"F0.wireOp",EDGE,"E23"),sQuery(id+"F0.wireOp",EDGE,"E28"),sQuery(id+"F0.wireOp",EDGE,"E29"),sQuery(id+"F0.wireOp",EDGE,"E30.0.MirrorC"),sQuery(id+"F0.wireOp",EDGE,"E30.1.MirrorC"),sQuery(id+"F0.wireOp",EDGE,"E31.0.MirrorC"),sQuery(id+"F0.wireOp",EDGE,"E31.1.MirrorC")])],"isStart":false})],"blendedInto":[makeQuery(id+"F1.opExtrude","CAP_FACE",FACE,{"disambiguationData":[OSD([subQ0,subQ1,sQuery(id+"F0.wireOp",EDGE,"E2"),sQuery(id+"F0.wireOp",EDGE,"E3"),sQuery(id+"F0.wireOp",EDGE,"E4"),sQuery(id+"F0.wireOp",EDGE,"E5"),sQuery(id+"F0.wireOp",EDGE,"E6"),sQuery(id+"F0.wireOp",EDGE,"E7"),sQuery(id+"F0.wireOp",EDGE,"E8"),sQuery(id+"F0.wireOp",EDGE,"E9"),sQuery(id+"F0.wireOp",EDGE,"E10"),sQuery(id+"F0.wireOp",EDGE,"E11"),sQuery(id+"F0.wireOp",EDGE,"E12"),sQuery(id+"F0.wireOp",EDGE,"E13"),sQuery(id+"F0.wireOp",EDGE,"E14"),sQuery(id+"F0.wireOp",EDGE,"E15"),sQuery(id+"F0.wireOp",EDGE,"E16"),sQuery(id+"F0.wireOp",EDGE,"E17"),sQuery(id+"F0.wireOp",EDGE,"E18"),sQuery(id+"F0.wireOp",EDGE,"E19"),sQuery(id+"F0.wireOp",EDGE,"E22"),sQuery(id+"F0.wireOp",EDGE,"E23"),sQuery(id+"F0.wireOp",EDGE,"E28"),sQuery(id+"F0.wireOp",EDGE,"E29"),sQuery(id+"F0.wireOp",EDGE,"E30.0.MirrorC"),sQuery(id+"F0.wireOp",EDGE,"E30.1.MirrorC"),sQuery(id+"F0.wireOp",EDGE,"E31.0.MirrorC"),sQuery(id+"F0.wireOp",EDGE,"E31.1.MirrorC")])],"isStart":false})]});}
            var Q36;
            {var subQ0=sQuery(id+"F0.wireOp",EDGE,"E3");var subQ1=sQuery(id+"F0.wireOp",EDGE,"E4");Q36=makeQuery(id+"F2.opFillet","BLEND_EDGE",EDGE,{"blendedFrom":[makeQuery(id+"F1.opExtrude","SWEPT_EDGE",EDGE,{"disambiguationData":[OSD([subQ0,subQ1])]}),makeQuery(id+"F1.opExtrude","CAP_FACE",FACE,{"disambiguationData":[OSD([sQuery(id+"F0.wireOp",EDGE,"E0"),sQuery(id+"F0.wireOp",EDGE,"E1"),sQuery(id+"F0.wireOp",EDGE,"E2"),subQ0,subQ1,sQuery(id+"F0.wireOp",EDGE,"E5"),sQuery(id+"F0.wireOp",EDGE,"E6"),sQuery(id+"F0.wireOp",EDGE,"E7"),sQuery(id+"F0.wireOp",EDGE,"E8"),sQuery(id+"F0.wireOp",EDGE,"E9"),sQuery(id+"F0.wireOp",EDGE,"E10"),sQuery(id+"F0.wireOp",EDGE,"E11"),sQuery(id+"F0.wireOp",EDGE,"E12"),sQuery(id+"F0.wireOp",EDGE,"E13"),sQuery(id+"F0.wireOp",EDGE,"E14"),sQuery(id+"F0.wireOp",EDGE,"E15"),sQuery(id+"F0.wireOp",EDGE,"E16"),sQuery(id+"F0.wireOp",EDGE,"E17"),sQuery(id+"F0.wireOp",EDGE,"E18"),sQuery(id+"F0.wireOp",EDGE,"E19"),sQuery(id+"F0.wireOp",EDGE,"E22"),sQuery(id+"F0.wireOp",EDGE,"E23"),sQuery(id+"F0.wireOp",EDGE,"E28"),sQuery(id+"F0.wireOp",EDGE,"E29"),sQuery(id+"F0.wireOp",EDGE,"E30.0.MirrorC"),sQuery(id+"F0.wireOp",EDGE,"E30.1.MirrorC"),sQuery(id+"F0.wireOp",EDGE,"E31.0.MirrorC"),sQuery(id+"F0.wireOp",EDGE,"E31.1.MirrorC")])],"isStart":false})],"blendedInto":[makeQuery(id+"F1.opExtrude","CAP_FACE",FACE,{"disambiguationData":[OSD([sQuery(id+"F0.wireOp",EDGE,"E0"),sQuery(id+"F0.wireOp",EDGE,"E1"),sQuery(id+"F0.wireOp",EDGE,"E2"),subQ0,subQ1,sQuery(id+"F0.wireOp",EDGE,"E5"),sQuery(id+"F0.wireOp",EDGE,"E6"),sQuery(id+"F0.wireOp",EDGE,"E7"),sQuery(id+"F0.wireOp",EDGE,"E8"),sQuery(id+"F0.wireOp",EDGE,"E9"),sQuery(id+"F0.wireOp",EDGE,"E10"),sQuery(id+"F0.wireOp",EDGE,"E11"),sQuery(id+"F0.wireOp",EDGE,"E12"),sQuery(id+"F0.wireOp",EDGE,"E13"),sQuery(id+"F0.wireOp",EDGE,"E14"),sQuery(id+"F0.wireOp",EDGE,"E15"),sQuery(id+"F0.wireOp",EDGE,"E16"),sQuery(id+"F0.wireOp",EDGE,"E17"),sQuery(id+"F0.wireOp",EDGE,"E18"),sQuery(id+"F0.wireOp",EDGE,"E19"),sQuery(id+"F0.wireOp",EDGE,"E22"),sQuery(id+"F0.wireOp",EDGE,"E23"),sQuery(id+"F0.wireOp",EDGE,"E28"),sQuery(id+"F0.wireOp",EDGE,"E29"),sQuery(id+"F0.wireOp",EDGE,"E30.0.MirrorC"),sQuery(id+"F0.wireOp",EDGE,"E30.1.MirrorC"),sQuery(id+"F0.wireOp",EDGE,"E31.0.MirrorC"),sQuery(id+"F0.wireOp",EDGE,"E31.1.MirrorC")])],"isStart":false})]});}
            var Q37;
            Q37=makeQuery(id+"F1.opExtrude","CAP_EDGE",EDGE,{"disambiguationData":[OSD([sQuery(id+"F0.wireOp",EDGE,"E23")])],"isStart":false});
            var Q38;
            Q38=makeQuery(id+"F1.opExtrude","CAP_EDGE",EDGE,{"disambiguationData":[OSD([sQuery(id+"F0.wireOp",EDGE,"E4")])],"isStart":false});
            var Q39;
            {var subQ0=sQuery(id+"F0.wireOp",EDGE,"E0");var subQ1=sQuery(id+"F0.wireOp",EDGE,"E19");Q39=makeQuery(id+"F2.opFillet","BLEND_EDGE",EDGE,{"blendedFrom":[makeQuery(id+"F1.opExtrude","SWEPT_EDGE",EDGE,{"disambiguationData":[OSD([subQ0,subQ1])]}),makeQuery(id+"F1.opExtrude","CAP_FACE",FACE,{"disambiguationData":[OSD([subQ0,sQuery(id+"F0.wireOp",EDGE,"E1"),sQuery(id+"F0.wireOp",EDGE,"E2"),sQuery(id+"F0.wireOp",EDGE,"E3"),sQuery(id+"F0.wireOp",EDGE,"E4"),sQuery(id+"F0.wireOp",EDGE,"E5"),sQuery(id+"F0.wireOp",EDGE,"E6"),sQuery(id+"F0.wireOp",EDGE,"E7"),sQuery(id+"F0.wireOp",EDGE,"E8"),sQuery(id+"F0.wireOp",EDGE,"E9"),sQuery(id+"F0.wireOp",EDGE,"E10"),sQuery(id+"F0.wireOp",EDGE,"E11"),sQuery(id+"F0.wireOp",EDGE,"E12"),sQuery(id+"F0.wireOp",EDGE,"E13"),sQuery(id+"F0.wireOp",EDGE,"E14"),sQuery(id+"F0.wireOp",EDGE,"E15"),sQuery(id+"F0.wireOp",EDGE,"E16"),sQuery(id+"F0.wireOp",EDGE,"E17"),sQuery(id+"F0.wireOp",EDGE,"E18"),subQ1,sQuery(id+"F0.wireOp",EDGE,"E22"),sQuery(id+"F0.wireOp",EDGE,"E23"),sQuery(id+"F0.wireOp",EDGE,"E28"),sQuery(id+"F0.wireOp",EDGE,"E29"),sQuery(id+"F0.wireOp",EDGE,"E30.0.MirrorC"),sQuery(id+"F0.wireOp",EDGE,"E30.1.MirrorC"),sQuery(id+"F0.wireOp",EDGE,"E31.0.MirrorC"),sQuery(id+"F0.wireOp",EDGE,"E31.1.MirrorC")])],"isStart":false})],"blendedInto":[makeQuery(id+"F1.opExtrude","CAP_FACE",FACE,{"disambiguationData":[OSD([subQ0,sQuery(id+"F0.wireOp",EDGE,"E1"),sQuery(id+"F0.wireOp",EDGE,"E2"),sQuery(id+"F0.wireOp",EDGE,"E3"),sQuery(id+"F0.wireOp",EDGE,"E4"),sQuery(id+"F0.wireOp",EDGE,"E5"),sQuery(id+"F0.wireOp",EDGE,"E6"),sQuery(id+"F0.wireOp",EDGE,"E7"),sQuery(id+"F0.wireOp",EDGE,"E8"),sQuery(id+"F0.wireOp",EDGE,"E9"),sQuery(id+"F0.wireOp",EDGE,"E10"),sQuery(id+"F0.wireOp",EDGE,"E11"),sQuery(id+"F0.wireOp",EDGE,"E12"),sQuery(id+"F0.wireOp",EDGE,"E13"),sQuery(id+"F0.wireOp",EDGE,"E14"),sQuery(id+"F0.wireOp",EDGE,"E15"),sQuery(id+"F0.wireOp",EDGE,"E16"),sQuery(id+"F0.wireOp",EDGE,"E17"),sQuery(id+"F0.wireOp",EDGE,"E18"),subQ1,sQuery(id+"F0.wireOp",EDGE,"E22"),sQuery(id+"F0.wireOp",EDGE,"E23"),sQuery(id+"F0.wireOp",EDGE,"E28"),sQuery(id+"F0.wireOp",EDGE,"E29"),sQuery(id+"F0.wireOp",EDGE,"E30.0.MirrorC"),sQuery(id+"F0.wireOp",EDGE,"E30.1.MirrorC"),sQuery(id+"F0.wireOp",EDGE,"E31.0.MirrorC"),sQuery(id+"F0.wireOp",EDGE,"E31.1.MirrorC")])],"isStart":false})]});}
            var Q40;
            {var subQ0=sQuery(id+"F0.wireOp",EDGE,"E4");var subQ1=sQuery(id+"F0.wireOp",EDGE,"E5");Q40=makeQuery(id+"F2.opFillet","BLEND_EDGE",EDGE,{"blendedFrom":[makeQuery(id+"F1.opExtrude","SWEPT_EDGE",EDGE,{"disambiguationData":[OSD([subQ0,subQ1])]}),makeQuery(id+"F1.opExtrude","CAP_FACE",FACE,{"disambiguationData":[OSD([sQuery(id+"F0.wireOp",EDGE,"E0"),sQuery(id+"F0.wireOp",EDGE,"E1"),sQuery(id+"F0.wireOp",EDGE,"E2"),sQuery(id+"F0.wireOp",EDGE,"E3"),subQ0,subQ1,sQuery(id+"F0.wireOp",EDGE,"E6"),sQuery(id+"F0.wireOp",EDGE,"E7"),sQuery(id+"F0.wireOp",EDGE,"E8"),sQuery(id+"F0.wireOp",EDGE,"E9"),sQuery(id+"F0.wireOp",EDGE,"E10"),sQuery(id+"F0.wireOp",EDGE,"E11"),sQuery(id+"F0.wireOp",EDGE,"E12"),sQuery(id+"F0.wireOp",EDGE,"E13"),sQuery(id+"F0.wireOp",EDGE,"E14"),sQuery(id+"F0.wireOp",EDGE,"E15"),sQuery(id+"F0.wireOp",EDGE,"E16"),sQuery(id+"F0.wireOp",EDGE,"E17"),sQuery(id+"F0.wireOp",EDGE,"E18"),sQuery(id+"F0.wireOp",EDGE,"E19"),sQuery(id+"F0.wireOp",EDGE,"E22"),sQuery(id+"F0.wireOp",EDGE,"E23"),sQuery(id+"F0.wireOp",EDGE,"E28"),sQuery(id+"F0.wireOp",EDGE,"E29"),sQuery(id+"F0.wireOp",EDGE,"E30.0.MirrorC"),sQuery(id+"F0.wireOp",EDGE,"E30.1.MirrorC"),sQuery(id+"F0.wireOp",EDGE,"E31.0.MirrorC"),sQuery(id+"F0.wireOp",EDGE,"E31.1.MirrorC")])],"isStart":false})],"blendedInto":[makeQuery(id+"F1.opExtrude","CAP_FACE",FACE,{"disambiguationData":[OSD([sQuery(id+"F0.wireOp",EDGE,"E0"),sQuery(id+"F0.wireOp",EDGE,"E1"),sQuery(id+"F0.wireOp",EDGE,"E2"),sQuery(id+"F0.wireOp",EDGE,"E3"),subQ0,subQ1,sQuery(id+"F0.wireOp",EDGE,"E6"),sQuery(id+"F0.wireOp",EDGE,"E7"),sQuery(id+"F0.wireOp",EDGE,"E8"),sQuery(id+"F0.wireOp",EDGE,"E9"),sQuery(id+"F0.wireOp",EDGE,"E10"),sQuery(id+"F0.wireOp",EDGE,"E11"),sQuery(id+"F0.wireOp",EDGE,"E12"),sQuery(id+"F0.wireOp",EDGE,"E13"),sQuery(id+"F0.wireOp",EDGE,"E14"),sQuery(id+"F0.wireOp",EDGE,"E15"),sQuery(id+"F0.wireOp",EDGE,"E16"),sQuery(id+"F0.wireOp",EDGE,"E17"),sQuery(id+"F0.wireOp",EDGE,"E18"),sQuery(id+"F0.wireOp",EDGE,"E19"),sQuery(id+"F0.wireOp",EDGE,"E22"),sQuery(id+"F0.wireOp",EDGE,"E23"),sQuery(id+"F0.wireOp",EDGE,"E28"),sQuery(id+"F0.wireOp",EDGE,"E29"),sQuery(id+"F0.wireOp",EDGE,"E30.0.MirrorC"),sQuery(id+"F0.wireOp",EDGE,"E30.1.MirrorC"),sQuery(id+"F0.wireOp",EDGE,"E31.0.MirrorC"),sQuery(id+"F0.wireOp",EDGE,"E31.1.MirrorC")])],"isStart":false})]});}
            var Q41;
            Q41=makeQuery(id+"F1.opExtrude","CAP_EDGE",EDGE,{"disambiguationData":[OSD([sQuery(id+"F0.wireOp",EDGE,"E5")])],"isStart":false});
            var Q42;
            Q42=makeQuery(id+"F1.opExtrude","CAP_EDGE",EDGE,{"disambiguationData":[OSD([sQuery(id+"F0.wireOp",EDGE,"E0")])],"isStart":false});
            var Q43;
            Q43=makeQuery(id+"F1.opExtrude","CAP_EDGE",EDGE,{"disambiguationData":[OSD([sQuery(id+"F0.wireOp",EDGE,"E19")])],"isStart":false});
            var Q44;
            Q44=makeQuery(id+"F1.opExtrude","CAP_EDGE",EDGE,{"disambiguationData":[OSD([sQuery(id+"F0.wireOp",EDGE,"E22")])],"isStart":false});
            var Q45;
            Q45=makeQuery(id+"F1.opExtrude","CAP_EDGE",EDGE,{"disambiguationData":[OSD([sQuery(id+"F0.wireOp",EDGE,"E31.1.MirrorC")])],"isStart":false});
            var Q46;
            Q46=makeQuery(id+"F1.opExtrude","CAP_EDGE",EDGE,{"disambiguationData":[OSD([sQuery(id+"F0.wireOp",EDGE,"E1")])],"isStart":false});
            var Q47;
            Q47=makeQuery(id+"F1.opExtrude","CAP_EDGE",EDGE,{"disambiguationData":[OSD([sQuery(id+"F0.wireOp",EDGE,"E3")])],"isStart":false});
            chamfer(context, id + "F3", {"entities" : qUnion([Q0, Q1, Q2, Q3, Q4, Q5, Q6, Q7, Q8, Q9, Q10, Q11, Q12, Q13, Q14, Q15, Q16, Q17, Q18, Q19, Q20, Q21, Q22, Q23, Q24, Q25, Q26, Q27, Q28, Q29, Q30, Q31, Q32, Q33, Q34, Q35, Q36, Q37, Q38, Q39, Q40, Q41, Q42, Q43, Q44, Q45, Q46, Q47]), "width" : 1 * mm, "tangentPropagation" : true});
        }
        {
            var Q0;
            Q0=makeQuery(id+"F0.imprint","IMPRINT",FACE,{"disambiguationData":[TD([[makeQuery(id+"F0.imprint","IMPRINT",EDGE,{"derivedFrom":sQuery(id+"F0.wireOp",EDGE,"E0")}),-1.0]])]});
            extrude(context, id + "F4", {"entities" : qUnion([Q0]), "depth" : 25 * mm});
        }
        {
            var Q0;
            Q0=makeQuery(id+"F4.opExtrude","SWEPT_EDGE",EDGE,{"disambiguationData":[OSD([sQuery(id+"F0.wireOp",EDGE,"E0"),sQuery(id+"F0.wireOp",EDGE,"E19")])]});
            var Q1;
            Q1=makeQuery(id+"F4.opExtrude","SWEPT_EDGE",EDGE,{"disambiguationData":[OSD([sQuery(id+"F0.wireOp",EDGE,"E0"),sQuery(id+"F0.wireOp",EDGE,"E1")])]});
            var Q2;
            Q2=makeQuery(id+"F4.opExtrude","SWEPT_EDGE",EDGE,{"disambiguationData":[OSD([sQuery(id+"F0.wireOp",EDGE,"E2"),sQuery(id+"F0.wireOp",EDGE,"E3")])]});
            var Q3;
            Q3=makeQuery(id+"F4.opExtrude","SWEPT_EDGE",EDGE,{"disambiguationData":[OSD([sQuery(id+"F0.wireOp",EDGE,"E3"),sQuery(id+"F0.wireOp",EDGE,"E4")])]});
            var Q4;
            Q4=makeQuery(id+"F4.opExtrude","SWEPT_EDGE",EDGE,{"disambiguationData":[OSD([sQuery(id+"F0.wireOp",EDGE,"E4"),sQuery(id+"F0.wireOp",EDGE,"E5")])]});
            var Q5;
            Q5=makeQuery(id+"F4.opExtrude","SWEPT_EDGE",EDGE,{"disambiguationData":[OSD([sQuery(id+"F0.wireOp",EDGE,"E8"),sQuery(id+"F0.wireOp",EDGE,"E9")])]});
            var Q6;
            Q6=makeQuery(id+"F4.opExtrude","SWEPT_EDGE",EDGE,{"disambiguationData":[OSD([sQuery(id+"F0.wireOp",EDGE,"E16"),sQuery(id+"F0.wireOp",EDGE,"E17")])]});
            var Q7;
            Q7=makeQuery(id+"F4.opExtrude","SWEPT_EDGE",EDGE,{"disambiguationData":[OSD([sQuery(id+"F0.wireOp",EDGE,"E15"),sQuery(id+"F0.wireOp",EDGE,"E16")])]});
            var Q8;
            Q8=makeQuery(id+"F4.opExtrude","SWEPT_EDGE",EDGE,{"disambiguationData":[OSD([sQuery(id+"F0.wireOp",EDGE,"E10"),sQuery(id+"F0.wireOp",EDGE,"E11")])]});
            var Q9;
            Q9=makeQuery(id+"F4.opExtrude","SWEPT_EDGE",EDGE,{"disambiguationData":[OSD([sQuery(id+"F0.wireOp",EDGE,"E14"),sQuery(id+"F0.wireOp",EDGE,"E15")])]});
            var Q10;
            Q10=makeQuery(id+"F4.opExtrude","SWEPT_EDGE",EDGE,{"disambiguationData":[OSD([sQuery(id+"F0.wireOp",EDGE,"E1"),sQuery(id+"F0.wireOp",EDGE,"E2")])]});
            var Q11;
            Q11=makeQuery(id+"F4.opExtrude","SWEPT_EDGE",EDGE,{"disambiguationData":[OSD([sQuery(id+"F0.wireOp",EDGE,"E5"),sQuery(id+"F0.wireOp",EDGE,"E6")])]});
            var Q12;
            Q12=makeQuery(id+"F4.opExtrude","SWEPT_EDGE",EDGE,{"disambiguationData":[OSD([sQuery(id+"F0.wireOp",EDGE,"E7"),sQuery(id+"F0.wireOp",EDGE,"E8")])]});
            var Q13;
            Q13=makeQuery(id+"F4.opExtrude","SWEPT_EDGE",EDGE,{"disambiguationData":[OSD([sQuery(id+"F0.wireOp",EDGE,"E13"),sQuery(id+"F0.wireOp",EDGE,"E14")])]});
            var Q14;
            Q14=makeQuery(id+"F4.opExtrude","SWEPT_EDGE",EDGE,{"disambiguationData":[OSD([sQuery(id+"F0.wireOp",EDGE,"E9"),sQuery(id+"F0.wireOp",EDGE,"E10")])]});
            var Q15;
            Q15=makeQuery(id+"F4.opExtrude","SWEPT_EDGE",EDGE,{"disambiguationData":[OSD([sQuery(id+"F0.wireOp",EDGE,"E6"),sQuery(id+"F0.wireOp",EDGE,"E7")])]});
            var Q16;
            Q16=makeQuery(id+"F4.opExtrude","SWEPT_EDGE",EDGE,{"disambiguationData":[OSD([sQuery(id+"F0.wireOp",EDGE,"E18"),sQuery(id+"F0.wireOp",EDGE,"E19")])]});
            var Q17;
            Q17=makeQuery(id+"F4.opExtrude","SWEPT_EDGE",EDGE,{"disambiguationData":[OSD([sQuery(id+"F0.wireOp",EDGE,"E12"),sQuery(id+"F0.wireOp",EDGE,"E13")])]});
            var Q18;
            Q18=makeQuery(id+"F4.opExtrude","SWEPT_EDGE",EDGE,{"disambiguationData":[OSD([sQuery(id+"F0.wireOp",EDGE,"E11"),sQuery(id+"F0.wireOp",EDGE,"E12")])]});
            var Q19;
            Q19=makeQuery(id+"F4.opExtrude","SWEPT_EDGE",EDGE,{"disambiguationData":[OSD([sQuery(id+"F0.wireOp",EDGE,"E17"),sQuery(id+"F0.wireOp",EDGE,"E18")])]});
            fillet(context, id + "F5", {"entities" : qUnion([Q0, Q1, Q2, Q3, Q4, Q5, Q6, Q7, Q8, Q9, Q10, Q11, Q12, Q13, Q14, Q15, Q16, Q17, Q18, Q19]), "radius" : 10 * mm, "tangentPropagation" : true, "allowEdgeOverflow" : false});
        }
    });
